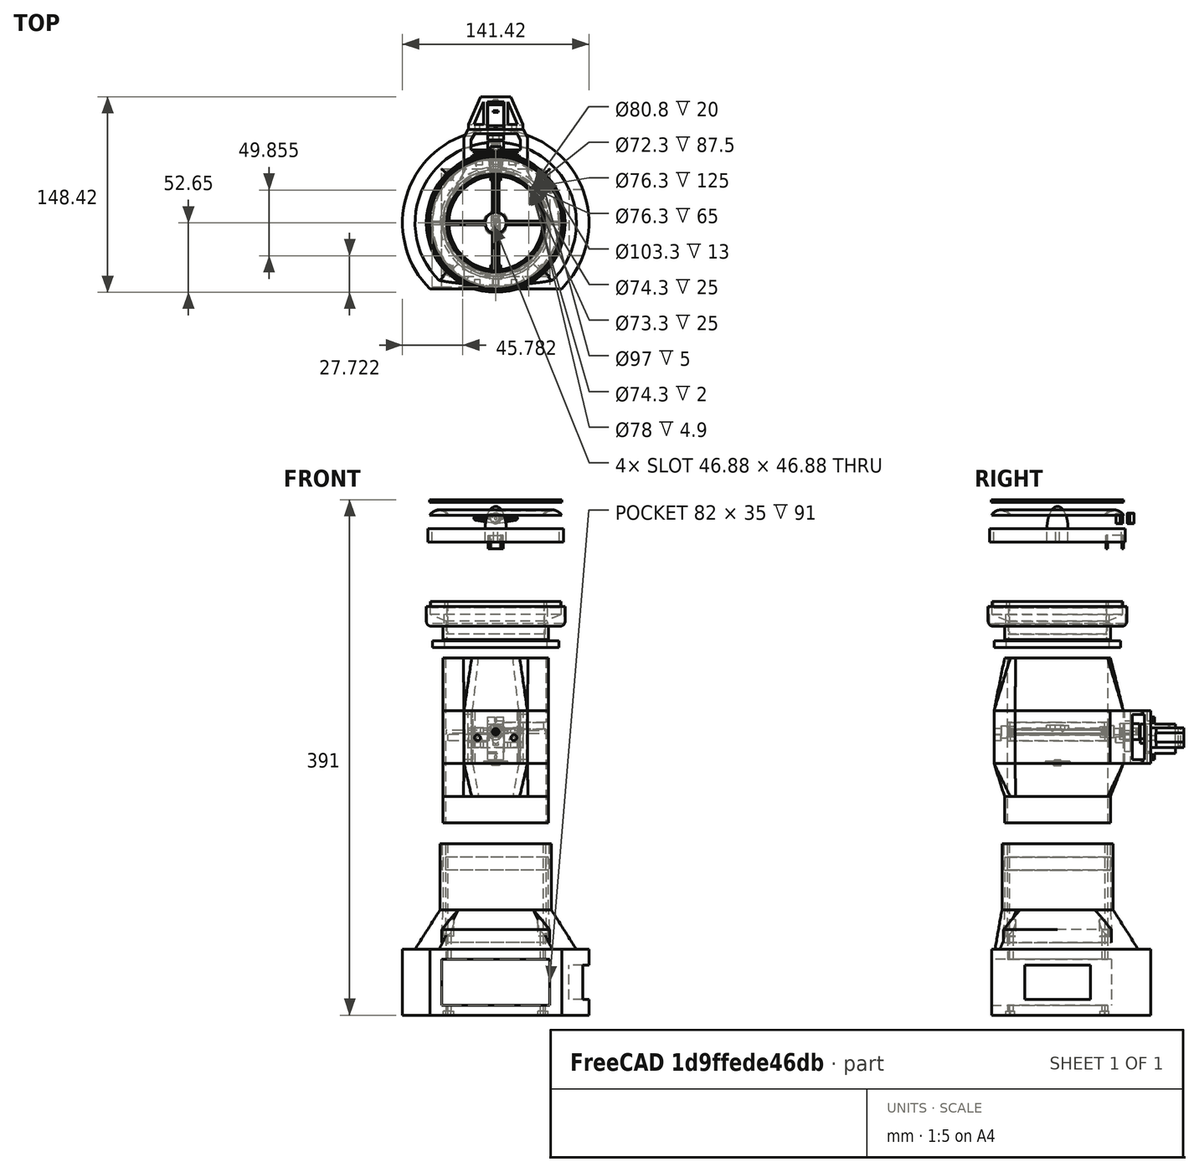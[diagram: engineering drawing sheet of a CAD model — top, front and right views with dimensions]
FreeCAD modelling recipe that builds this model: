
FCSTD DOCUMENT  (FreeCAD 0.20R29177 (Git))
Label: WindSim (1) (2) (1) (1)
License: All rights reserved
LicenseURL: http://en.wikipedia.org/wiki/All_rights_reserved
objects: Sketcher::SketchObject×66, PartDesign::Pocket×28, PartDesign::Pad×23, PartDesign::Body×14, PartDesign::AdditiveLoft×5, PartDesign::Mirrored×4, Part::Feature×4, App::DocumentObjectGroup×3, PartDesign::Revolution×2, Part::Part2DObjectPython×1, PartDesign::PolarPattern×1, PartDesign::Fillet×1, Spreadsheet::Sheet×1, Mesh::Feature×1
note: 208 computed .brp shape members not serialized (recipe doc carries the construction recipe); baked Part::Feature solids carry a one-line shape summary decoded from their .brp

FEATURE [Sketcher::SketchObject] Sketch004  label="sk_flap_base"
  FullyConstrained = true
  MapMode = 5
  Support = -> [XY_Plane001]
  expr: .Constraints.flap_diameter = <<Spreadsheet>>.flap_diameter
  sketch-geometry (1):
    g0: Circle CenterX=0 CenterY=0 CenterZ=0 NormalX=0 NormalY=0 NormalZ=1 AngleXU=0 Radius=37.65
  constraints (2):
    c: Coincident(g0,g-1)
    c: Diameter(g0) = 75.3  'flap_diameter'
FEATURE [PartDesign::Pad] Pad002  label="pad_flap_base"
  Direction = (0,0,1)
  Length = 2
  Length2 = 10
  Profile = -> Sketch004
  Type = 0
  expr: Length = <<Spreadsheet>>.flap_width
FEATURE [Sketcher::SketchObject] Sketch005  label="sk_flap_rod"
  AttachmentOffset = pos=(0,1,0) rot=(0,0,1;0rad)
  FullyConstrained = true
  MapMode = 5
  Placement = pos=(-2e-16,2e-16,1) rot=(0.57735,0.57735,0.57735;2.0944rad)
  Support = -> [YZ_Plane001]
  expr: .AttachmentOffset.Base.y = <<pad_flap_base>>.Length / 2
  expr: .Constraints.flap_rod_hole_diameter = <<Spreadsheet>>.flap_rod_hole_diameter
  expr: .Constraints.flap_rod_outer_diameter = <<Spreadsheet>>.flap_rod_hole_diameter + <<Spreadsheet>>.flap_rod_width
  sketch-geometry (2):
    g0: Circle CenterX=0 CenterY=0 CenterZ=0 NormalX=0 NormalY=0 NormalZ=1 AngleXU=0 Radius=1.75
    g1: Circle CenterX=0 CenterY=0 CenterZ=0 NormalX=0 NormalY=0 NormalZ=1 AngleXU=0 Radius=2.75
  constraints (4):
    c: Coincident(g0,g-1)
    c: Coincident(g1,g0)
    c: Diameter(g0) = 3.5  'flap_rod_hole_diameter'
    c: Diameter(g1) = 5.5  'flap_rod_outer_diameter'
FEATURE [PartDesign::Pad] Pad003  label="pad_flap_rod"
  BaseFeature = -> Pad002
  Direction = (1,-2e-16,3e-16)
  Length = 65.3
  Length2 = 10
  Midplane = true
  Profile = -> Sketch005
  Type = 0
  expr: Length = <<Spreadsheet>>.flap_diameter - 10mm
FEATURE [Sketcher::SketchObject] Sketch006  label="sk_flap_rod_hole_through"
  AttachmentOffset = pos=(0,1,37.65) rot=(0,0,1;0rad)
  FullyConstrained = true
  MapMode = 5
  Placement = pos=(37.65,-8.1e-15,1) rot=(0.57735,0.57735,0.57735;2.0944rad)
  Support = -> [YZ_Plane001]
  expr: .AttachmentOffset.Base.y = <<pad_flap_base>>.Length / 2
  expr: .AttachmentOffset.Base.z = <<sk_flap_base>>.Constraints.flap_diameter / 2
  expr: .Constraints.flap_rod_hole_diameter = <<sk_flap_rod>>.Constraints.flap_rod_hole_diameter
  sketch-geometry (1):
    g0: Circle CenterX=0 CenterY=0 CenterZ=0 NormalX=0 NormalY=0 NormalZ=1 AngleXU=0 Radius=1.75
  constraints (2):
    c: Coincident(g0,g-1)
    c: Diameter(g0) = 3.5  'flap_rod_hole_diameter'
FEATURE [Sketcher::SketchObject] Sketch007  label="sk_flap_rod_hold"
  AttachmentOffset = pos=(0,1,37.15) rot=(0,0,1;0rad)
  FullyConstrained = true
  MapMode = 5
  Placement = pos=(37.15,-8e-15,1) rot=(0.57735,0.57735,0.57735;2.0944rad)
  Support = -> [YZ_Plane001]
  expr: .AttachmentOffset.Base.y = <<pad_flap_base>>.Length / 2
  expr: .AttachmentOffset.Base.z = <<sk_flap_base>>.Constraints.flap_diameter / 2 - 0.5mm
  expr: Constraints[1] = <<Spreadsheet>>.flap_rod_nut_width + 2mm
  sketch-geometry (1):
    g0: Circle CenterX=0 CenterY=0 CenterZ=0 NormalX=0 NormalY=0 NormalZ=1 AngleXU=0 Radius=4.05
  constraints (2):
    c: Coincident(g0,g-1)
    c: Diameter(g0) = 8.1
FEATURE [PartDesign::Pad] Pad004  label="pad_flap_hold"
  BaseFeature = -> Pad003
  Direction = (1,-2e-16,3e-16)
  Length = 5
  Length2 = 10
  Profile = -> Sketch007
  Reversed = true
  Type = 0
FEATURE [Sketcher::SketchObject] Sketch008  label="sk_flap_nut_hold"
  AttachmentOffset = pos=(0,1,37.65) rot=(0,0,1;0rad)
  FullyConstrained = true
  MapMode = 5
  Placement = pos=(37.65,-8.1e-15,1) rot=(0.57735,0.57735,0.57735;2.0944rad)
  Support = -> [YZ_Plane001]
  expr: .AttachmentOffset.Base.y = <<pad_flap_base>>.Length / 2
  expr: .AttachmentOffset.Base.z = <<sk_flap_base>>.Constraints.flap_diameter / 2
  expr: Constraints[19] = <<Spreadsheet>>.flap_rod_nut_width
  sketch-geometry (7):
    g0: LineSegment StartX=1.525 StartY=-2.64138 StartZ=0 EndX=3.05 EndY=4e-16 EndZ=0
    g1: LineSegment StartX=3.05 StartY=4e-16 StartZ=0 EndX=1.525 EndY=2.64138 EndZ=0
    g2: LineSegment StartX=1.525 StartY=2.64138 StartZ=0 EndX=-1.525 EndY=2.64138 EndZ=0
    g3: LineSegment StartX=-1.525 StartY=2.64138 StartZ=0 EndX=-3.05 EndY=4e-16 EndZ=0
    g4: LineSegment StartX=-3.05 StartY=4e-16 StartZ=0 EndX=-1.525 EndY=-2.64138 EndZ=0
    g5: LineSegment StartX=-1.525 StartY=-2.64138 StartZ=0 EndX=1.525 EndY=-2.64138 EndZ=0
    g6: Circle CenterX=0 CenterY=0 CenterZ=0 NormalX=0 NormalY=0 NormalZ=1 AngleXU=0 Radius=3.05
  constraints (16):
    c: Coincident(g0,g1)
    c: Coincident(g1,g2)
    c: Coincident(g2,g3)
    c: Coincident(g3,g4)
    c: Coincident(g4,g5)
    c: Coincident(g5,g0)
    c: Equal(g0, g1-g5) x5
    c: PointOnObject(g0,g6)
    c: PointOnObject(g1,g6)
    c: PointOnObject(g2,g6)
    c: PointOnObject(g3,g6)
    c: PointOnObject(g4,g6)
    c: PointOnObject(g5,g6)
    c: Coincident(g6,g-1)
    c: Horizontal(g5)
    c: DistanceX(g3,g0) = 6.1
FEATURE [PartDesign::Mirrored] Mirrored  label="mirror_flap_hold"
  BaseFeature = -> Pad004
  MirrorPlane = -> YZ_Plane001
  Originals = -> [Pad004]
FEATURE [PartDesign::Pocket] Pocket  label="pocket_nut_hold"
  BaseFeature = -> Mirrored
  Direction = (-1,2e-16,-3e-16)
  Length = 4
  Length2 = 5
  Profile = -> Sketch008
  Type = 0
FEATURE [PartDesign::Mirrored] Mirrored001  label="mirror_pocket_nut_hold"
  BaseFeature = -> Pocket
  MirrorPlane = -> YZ_Plane001
  Originals = -> [Pocket]
FEATURE [Sketcher::SketchObject] Sketch009  label="sk_valve_base"
  FullyConstrained = true
  MapMode = 5
  Support = -> [XY_Plane002]
  expr: Constraints[1] = <<sk_fanduct_base>>.Constraints.duct_hole_diameter
  expr: Constraints[3] = <<sk_pipe>>.Constraints.pipe_outer_diameter
  sketch-geometry (11):
    g0: Circle CenterX=0 CenterY=0 CenterZ=0 NormalX=0 NormalY=0 NormalZ=1 AngleXU=0 Radius=38.15
    g1: ArcOfCircle CenterX=0 CenterY=0 CenterZ=0 NormalX=0 NormalY=0 NormalZ=1 AngleXU=0 Radius=40.15 StartAngle=2.61815 EndAngle=4.07013
    g2: LineSegment StartX=17.5 StartY=50 StartZ=0 EndX=-17.5 EndY=50 EndZ=0
    g3: LineSegment StartX=-24.0499 StartY=-32.15 StartZ=0 EndX=-24.0499 EndY=-48.15 EndZ=0
    g4: LineSegment StartX=24.0499 StartY=-32.15 StartZ=0 EndX=24.0499 EndY=-48.15 EndZ=0
    g5: LineSegment StartX=24.0499 StartY=-48.15 StartZ=0 EndX=-24.0499 EndY=-48.15 EndZ=0
    g6: ArcOfCircle CenterX=0 CenterY=0 CenterZ=0 NormalX=0 NormalY=0 NormalZ=1 AngleXU=0 Radius=40.15 StartAngle=5.35464 EndAngle=6.80663
    g7: GeomPoint X=0 Y=38.15 Z=0
    g8: GeomPoint X=0 Y=-38.15 Z=0
    g9: LineSegment StartX=-17.5 StartY=50 StartZ=0 EndX=-34.7741 EndY=20.0695 EndZ=0
    g10: LineSegment StartX=17.5 StartY=50 StartZ=0 EndX=34.7741 EndY=20.0695 EndZ=0
  constraints (29):
    c: Coincident(g0,g-1)
    c: Diameter(g0) = 76.3
    c: Coincident(g1,g0)
    c: Diameter(g1) = 80.3
    c: Vertical(g3)
    c: Vertical(g4)
    c: Coincident(g5,g4)
    c: Coincident(g5,g3)
    c: Horizontal(g5)
    c: Symmetric(g4,g3,g-2)
    c: PointOnObject(g6,g4)
    c: Coincident(g1,g6)
    c: DistanceY(g4,g4) = 16  'bottom_hold_height'
    c: PointOnObject(g7,g0)
    c: PointOnObject(g7,g-2)
    c: PointOnObject(g8,g0)
    c: PointOnObject(g8,g-2)
    c: DistanceY(g3,g8) = 10
    c: DistanceY(g0,g2) = 50  'top_border'
    c: DistanceY(g4,g0) = 48.15  'bottom_border'
    c: Tangent(g1,g9) = -1.5708
    c: Tangent(g6,g10) = 1.5708
    c: Coincident(g9,g2)
    c: Coincident(g10,g2)
    c: Coincident(g3,g1)
    c: Horizontal(g2)
    c: Symmetric(g1,g6,g-2)
    c: DistanceX(g2,g2) = 35  'top_width'
    c: Angle(g9,g2) = 2.09424  'top_angle'
FEATURE [PartDesign::Pad] Pad005  label="pad_valve_base"
  Direction = (0,0,1)
  Length = 40
  Length2 = 10
  Profile = -> Sketch009
  Type = 0
FEATURE [Sketcher::SketchObject] Sketch011  label="sk_valve_front_taper"
  AttachmentOffset = pos=(0,0,80) rot=(0,0,1;0rad)
  FullyConstrained = true
  MapMode = 5
  Placement = pos=(0,0,80) rot=(0,0,1;0rad)
  Support = -> [XY_Plane002]
  expr: .AttachmentOffset.Base.z = <<pad_valve_base>>.Length + 40mm
  expr: Constraints[2] = <<sk_fanduct_base>>.Constraints.duct_hole_diameter
  expr: Constraints[3] = <<sk_pipe>>.Constraints.pipe_outer_diameter
  sketch-geometry (2):
    g0: Circle CenterX=0 CenterY=0 CenterZ=0 NormalX=0 NormalY=0 NormalZ=1 AngleXU=0 Radius=38.15
    g1: Circle CenterX=0 CenterY=0 CenterZ=0 NormalX=0 NormalY=0 NormalZ=1 AngleXU=0 Radius=40.15
  constraints (4):
    c: Coincident(g0,g-1)
    c: Coincident(g1,g0)
    c: Diameter(g0) = 76.3
    c: Diameter(g1) = 80.3
FEATURE [Part::Feature] Fusion007001  label="Servo-sg90-final"
  Placement = pos=(0,89.6,7.5) rot=(1,0,0;1.5708rad)
  shape: bbox 11.8 x 29.9 x 32.4 mm, 77 faces (baked)
FEATURE [Part::Feature] Pocket003001  label="Final-2-arms-horn"
  Placement = pos=(0,53,186) rot=(-1,0,0;1.5708rad)
  shape: bbox 33 x 5 x 8 mm, 28 faces (baked)
FEATURE [Part::Feature] Pocket003002  label="Final-2-arms-horn001"
  Placement = pos=(0,49.5,186) rot=(0,0.707107,-0.707107;3.14159rad)
  shape: bbox 33 x 5 x 8 mm, 28 faces (baked)
FEATURE [Sketcher::SketchObject] Sketch012  label="sk_valve_main_axis"
  AttachmentOffset = pos=(0,24,-50) rot=(0,0,1;0rad)
  FullyConstrained = true
  MapMode = 5
  Placement = pos=(0,50,24) rot=(1,0,0;1.5708rad)
  Support = -> [XZ_Plane002]
  expr: .AttachmentOffset.Base.z = Sketch009.Constraints.top_border * -1
  sketch-geometry (1):
    g0: Circle CenterX=0 CenterY=0 CenterZ=0 NormalX=0 NormalY=0 NormalZ=1 AngleXU=0 Radius=2.45
  constraints (2):
    c: Coincident(g0,g-1)
    c: Diameter(g0) = 4.9  'main_axis_diameter'
FEATURE [Sketcher::SketchObject] Sketch014  label="sk_bearing_top"
  AttachmentOffset = pos=(0,24,-37.65) rot=(0,0,1;0rad)
  FullyConstrained = true
  MapMode = 5
  Placement = pos=(0,37.65,24) rot=(1,0,0;1.5708rad)
  Support = -> [XZ_Plane002]
  expr: .AttachmentOffset.Base.z = <<sk_fanduct_base>>.Constraints.duct_hole_diameter / 2 * -1 + 0.5mm
  sketch-geometry (1):
    g0: Circle CenterX=0 CenterY=0 CenterZ=0 NormalX=0 NormalY=0 NormalZ=1 AngleXU=0 Radius=4.5
  constraints (2):
    c: Coincident(g0,g-1)
    c: Diameter(g0) = 9  'bearing_diameter'
FEATURE [PartDesign::Pocket] Pocket003003  label="pocket_valve_main_axis"
  BaseFeature = -> Pad005
  Direction = (0,1,2e-16)
  Length = 2
  Length2 = 5
  Midplane = true
  Profile = -> Sketch012
  Type = 1
FEATURE [PartDesign::Pocket] Pocket003004  label="pocket_bearing_top"
  BaseFeature = -> Pocket003003
  Direction = (0,1,2e-16)
  Length = 5
  Length2 = 5
  Profile = -> Sketch014
  Type = 0
FEATURE [Sketcher::SketchObject] Sketch015  label="sk_bearing_bottom"
  AttachmentOffset = pos=(0,24,37.65) rot=(0,0,1;0rad)
  FullyConstrained = true
  MapMode = 5
  Placement = pos=(0,-37.65,24) rot=(1,0,0;1.5708rad)
  Support = -> [XZ_Plane002]
  expr: .AttachmentOffset.Base.z = <<sk_fanduct_base>>.Constraints.duct_hole_diameter / 2 - 0.5mm
  expr: Constraints[1] = <<sk_bearing_top>>.Constraints.bearing_diameter
  sketch-geometry (1):
    g0: Circle CenterX=0 CenterY=0 CenterZ=0 NormalX=0 NormalY=0 NormalZ=1 AngleXU=0 Radius=4.5
  constraints (2):
    c: Coincident(g0,g-1)
    c: Diameter(g0) = 9
FEATURE [PartDesign::Pocket] Pocket003005  label="pocket_bearing_bottom"
  BaseFeature = -> Pocket003004
  Direction = (0,1,2e-16)
  Length = 5
  Length2 = 5
  Profile = -> Sketch015
  Reversed = true
  Type = 0
FEATURE [Sketcher::SketchObject] Sketch016  label="sk_valve_back_taper"
  AttachmentOffset = pos=(0,0,-25) rot=(0,0,1;0rad)
  FullyConstrained = true
  MapMode = 5
  Placement = pos=(0,0,-25) rot=(0,0,1;0rad)
  Support = -> [XY_Plane002]
  expr: Constraints[2] = <<sk_fanduct_base>>.Constraints.duct_hole_diameter
  expr: Constraints[3] = <<sk_pipe>>.Constraints.pipe_outer_diameter
  sketch-geometry (2):
    g0: Circle CenterX=0 CenterY=0 CenterZ=0 NormalX=0 NormalY=0 NormalZ=1 AngleXU=0 Radius=38.15
    g1: Circle CenterX=0 CenterY=0 CenterZ=0 NormalX=0 NormalY=0 NormalZ=1 AngleXU=0 Radius=40.15
  constraints (4):
    c: Coincident(g0,g-1)
    c: Coincident(g1,g0)
    c: Diameter(g0) = 76.3
    c: Diameter(g1) = 80.3
FEATURE [Part::Feature] Part__Feature  label="shaft-drill"
  shape: bbox 18.7 x 18.7 x 4.1 mm, 22 faces (baked)
FEATURE [Sketcher::SketchObject] Sketch020
  FullyConstrained = true
  MapMode = 5
  Support = -> [XY_Plane003]
  sketch-geometry (1):
    g0: Circle CenterX=0 CenterY=0 CenterZ=0 NormalX=0 NormalY=0 NormalZ=1 AngleXU=0 Radius=6
  constraints (2):
    c: Coincident(g0,g-1)
    c: Diameter(g0) = 12  'aussendurchmesser'
FEATURE [PartDesign::Pad] Pad008
  Direction = (1,1,1)
  Length = 3
  Length2 = 100
  Profile = -> Sketch020
  Type = 0
FEATURE [Part::Part2DObjectPython] InvoluteGear  # Draft 2D object (typed FeaturePython)
  ExternalGear = true
  HighPrecision = true
  Modules = 0.19
  NumberOfTeeth = 24
  PressureAngle = 28
FEATURE [PartDesign::Pocket] Pocket003007
  BaseFeature = -> Pad008
  Direction = (1,1,1)
  Length = 5
  Length2 = 100
  Profile = -> InvoluteGear
  Reversed = true
  Type = 1
FEATURE [Sketcher::SketchObject] Sketch021
  AttachmentOffset = pos=(0,0,3) rot=(0,0,1;0rad)
  FullyConstrained = true
  MapMode = 5
  Placement = pos=(0,0,3) rot=(0,0,1;0rad)
  Support = -> [XY_Plane003]
  expr: .AttachmentOffset.Base.z = <<Pad008>>.Length
  expr: Constraints[1] = <<Sketch020>>.Constraints.aussendurchmesser
  sketch-geometry (1):
    g0: Circle CenterX=0 CenterY=0 CenterZ=0 NormalX=0 NormalY=0 NormalZ=1 AngleXU=0 Radius=6
  constraints (2):
    c: Coincident(g0,g-1)
    c: Diameter(g0) = 12
FEATURE [PartDesign::Pad] Pad009
  BaseFeature = -> Pocket003007
  Direction = (1,1,1)
  Length = 12
  Length2 = 100
  Profile = -> Sketch021
  Type = 0
FEATURE [Sketcher::SketchObject] Sketch022
  AttachmentOffset = pos=(0,0,15) rot=(0,0,1;0rad)
  FullyConstrained = true
  MapMode = 5
  Placement = pos=(0,0,15) rot=(0,0,1;0rad)
  Support = -> [XY_Plane003]
  expr: .AttachmentOffset.Base.z = <<Pad008>>.Length + <<Pad009>>.Length
  sketch-geometry (7):
    g0: LineSegment StartX=1.525 StartY=-2.64138 StartZ=0 EndX=3.05 EndY=-1.332e-13 EndZ=0
    g1: LineSegment StartX=3.05 StartY=-1.332e-13 StartZ=0 EndX=1.525 EndY=2.64138 EndZ=0
    g2: LineSegment StartX=1.525 StartY=2.64138 StartZ=0 EndX=-1.525 EndY=2.64138 EndZ=0
    g3: LineSegment StartX=-1.525 StartY=2.64138 StartZ=0 EndX=-3.05 EndY=-1.248e-13 EndZ=0
    g4: LineSegment StartX=-3.05 StartY=-1.248e-13 StartZ=0 EndX=-1.525 EndY=-2.64138 EndZ=0
    g5: LineSegment StartX=-1.525 StartY=-2.64138 StartZ=0 EndX=1.525 EndY=-2.64138 EndZ=0
    g6: Circle CenterX=0 CenterY=0 CenterZ=0 NormalX=0 NormalY=0 NormalZ=1 AngleXU=0 Radius=3.05
  constraints (16):
    c: Coincident(g0,g1)
    c: Coincident(g1,g2)
    c: Coincident(g2,g3)
    c: Coincident(g3,g4)
    c: Coincident(g4,g5)
    c: Coincident(g5,g0)
    c: Equal(g0, g1-g5) x5
    c: PointOnObject(g0,g6)
    c: PointOnObject(g1,g6)
    c: PointOnObject(g2,g6)
    c: PointOnObject(g3,g6)
    c: PointOnObject(g4,g6)
    c: PointOnObject(g5,g6)
    c: Coincident(g6,g-1)
    c: Horizontal(g5)
    c: DistanceX(g3,g0) = 6.1
FEATURE [PartDesign::Pocket] Pocket003008
  BaseFeature = -> Pad009
  Direction = (1,1,1)
  Length = 7
  Length2 = 100
  Profile = -> Sketch022
  Type = 0
FEATURE [Sketcher::SketchObject] Sketch023
  AttachmentOffset = pos=(0,0,8) rot=(0,0,1;0rad)
  FullyConstrained = true
  MapMode = 5
  Placement = pos=(0,0,8) rot=(0,0,1;0rad)
  Support = -> [XY_Plane003]
  expr: .AttachmentOffset.Base.z = <<Pad008>>.Length + <<Pad009>>.Length - <<Pocket003008>>.Length
  sketch-geometry (1):
    g0: Circle CenterX=0 CenterY=0 CenterZ=0 NormalX=0 NormalY=0 NormalZ=1 AngleXU=0 Radius=1
  constraints (2):
    c: Coincident(g0,g-1)
    c: Diameter(g0) = 2
FEATURE [PartDesign::Pocket] Pocket003009
  BaseFeature = -> Pocket003008
  Direction = (1,1,1)
  Length = 4.8
  Length2 = 100
  Profile = -> Sketch023
  Type = 1
  expr: Length = 2.4 * 2
FEATURE [Sketcher::SketchObject] Sketch024
  ExternalGeometry = -> [Pocket003009]
  FullyConstrained = true
  MapMode = 5
  Support = -> [XY_Plane003]
  constraints (1):
    c: Distance(g-3,g-4) = 4.93975
FEATURE [PartDesign::Body] Body003  label="Servo_shaft_adapter"
  Group = -> [Sketch020,Pad008,InvoluteGear,Pocket003007,Sketch021,Pad009,Sketch022,Pocket003008,Sketch023,Pocket003009,Sketch024]
  Origin = -> Origin003
  Placement = pos=(0,47.3,24.1) rot=(-1,0,0;1.5708rad)
  Tip = -> Pocket003009
FEATURE [Sketcher::SketchObject] Sketch029  label="sk_valve_front"
  AttachmentOffset = pos=(0,0,40) rot=(0,0,1;0rad)
  FullyConstrained = true
  MapMode = 5
  Placement = pos=(0,0,40) rot=(0,0,1;0rad)
  Support = -> [XY_Plane002]
  expr: .AttachmentOffset.Base.z = <<pad_valve_base>>.Length
  expr: Constraints[1] = <<sk_fanduct_base>>.Constraints.duct_hole_diameter
  expr: Constraints[3] = <<sk_pipe>>.Constraints.pipe_outer_diameter
  sketch-geometry (11):
    g0: Circle CenterX=0 CenterY=0 CenterZ=0 NormalX=0 NormalY=0 NormalZ=1 AngleXU=0 Radius=38.15
    g1: ArcOfCircle CenterX=0 CenterY=0 CenterZ=0 NormalX=0 NormalY=0 NormalZ=1 AngleXU=0 Radius=40.15 StartAngle=2.61815 EndAngle=4.07013
    g2: LineSegment StartX=17.5 StartY=50 StartZ=0 EndX=-17.5 EndY=50 EndZ=0
    g3: LineSegment StartX=-24.0499 StartY=-32.15 StartZ=0 EndX=-24.0499 EndY=-48.15 EndZ=0
    g4: LineSegment StartX=24.0499 StartY=-32.15 StartZ=0 EndX=24.0499 EndY=-48.15 EndZ=0
    g5: LineSegment StartX=24.0499 StartY=-48.15 StartZ=0 EndX=-24.0499 EndY=-48.15 EndZ=0
    g6: ArcOfCircle CenterX=0 CenterY=0 CenterZ=0 NormalX=0 NormalY=0 NormalZ=1 AngleXU=0 Radius=40.15 StartAngle=5.35464 EndAngle=6.80663
    g7: GeomPoint X=0 Y=38.15 Z=0
    g8: GeomPoint X=0 Y=-38.15 Z=0
    g9: LineSegment StartX=-17.5 StartY=50 StartZ=0 EndX=-34.7741 EndY=20.0695 EndZ=0
    g10: LineSegment StartX=17.5 StartY=50 StartZ=0 EndX=34.7741 EndY=20.0695 EndZ=0
  constraints (28):
    c: Coincident(g0,g-1)
    c: Diameter(g0) = 76.3
    c: Coincident(g1,g0)
    c: Diameter(g1) = 80.3
    c: Vertical(g3)
    c: Vertical(g4)
    c: Coincident(g5,g4)
    c: Coincident(g5,g3)
    c: Horizontal(g5)
    c: Symmetric(g4,g3,g-2)
    c: PointOnObject(g6,g4)
    c: Coincident(g1,g6)
    c: DistanceY(g4,g4) = 16  'bottom_hold_height'
    c: PointOnObject(g7,g0)
    c: PointOnObject(g7,g-2)
    c: PointOnObject(g8,g0)
    c: PointOnObject(g8,g-2)
    c: DistanceY(g3,g8) = 10
    c: DistanceY(g0,g2) = 50  'top_border'
    c: DistanceY(g4,g0) = 48.15  'bottom_border'
    c: Tangent(g1,g9) = -1.5708
    c: Tangent(g6,g10) = 1.5708
    c: Coincident(g9,g2)
    c: Coincident(g10,g2)
    c: Coincident(g3,g1)
    c: Horizontal(g2)
    c: Symmetric(g1,g6,g-2)
    c: DistanceX(g2,g2) = 35  'top_width'
FEATURE [Sketcher::SketchObject] Sketch030  label="sk_flap_counter_right"
  AttachmentOffset = pos=(0,0,26) rot=(0,0,1;0rad)
  FullyConstrained = true
  MapMode = 5
  Placement = pos=(0,0,26) rot=(0,0,1;0rad)
  Support = -> [XY_Plane002]
  expr: Constraints[5] = <<sk_pipe>>.Constraints.pipe_outer_diameter
  sketch-geometry (4):
    g0: ArcOfCircle CenterX=0 CenterY=1.3e-15 CenterZ=0 NormalX=0 NormalY=0 NormalZ=1 AngleXU=0 Radius=40.15 StartAngle=4.83725 EndAngle=7.72912
    g1: ArcOfCircle CenterX=0 CenterY=1.3e-15 CenterZ=0 NormalX=0 NormalY=0 NormalZ=1 AngleXU=0 Radius=36.1846 StartAngle=4.85101 EndAngle=7.71536
    g2: LineSegment StartX=5 StartY=39.8375 StartZ=0 EndX=5 EndY=35.8375 EndZ=0
    g3: LineSegment StartX=5 StartY=-39.8375 StartZ=0 EndX=5 EndY=-35.8375 EndZ=0
  constraints (12):
    c: Coincident(g1,g0)
    c: Coincident(g2,g0)
    c: Coincident(g2,g1)
    c: Coincident(g3,g0)
    c: Coincident(g3,g1)
    c: Diameter(g0) = 80.3
    c: Symmetric(g1,g1,g-1)
    c: Vertical(g2)
    c: Vertical(g3)
    c: DistanceY(g2,g2) = 4  'inner_pad_height'
    c: DistanceX(g0,g0) = 5  'inner_pad_distance'
    c: Coincident(g0,g-1)
FEATURE [Sketcher::SketchObject] Sketch031  label="sk_flap_counter_left"
  AttachmentOffset = pos=(0,0,22) rot=(0,0,1;0rad)
  FullyConstrained = true
  MapMode = 5
  Placement = pos=(0,0,22) rot=(0,0,1;0rad)
  Support = -> [XY_Plane002]
  expr: Constraints[7] = <<sk_flap_counter_right>>.Constraints.inner_pad_height
  expr: Constraints[8] = <<sk_flap_counter_right>>.Constraints.inner_pad_distance
  expr: Constraints[9] = <<sk_pipe>>.Constraints.pipe_outer_diameter
  sketch-geometry (4):
    g0: ArcOfCircle CenterX=0 CenterY=-2.5e-15 CenterZ=0 NormalX=0 NormalY=0 NormalZ=1 AngleXU=0 Radius=36.1846 StartAngle=1.70942 EndAngle=4.57376
    g1: ArcOfCircle CenterX=0 CenterY=-2.5e-15 CenterZ=0 NormalX=0 NormalY=0 NormalZ=1 AngleXU=0 Radius=40.15 StartAngle=1.69565 EndAngle=4.58753
    g2: LineSegment StartX=-5 StartY=39.8375 StartZ=0 EndX=-5 EndY=35.8375 EndZ=0
    g3: LineSegment StartX=-5 StartY=-39.8375 StartZ=0 EndX=-5 EndY=-35.8375 EndZ=0
  constraints (12):
    c: Coincident(g1,g0)
    c: Coincident(g2,g1)
    c: Coincident(g2,g0)
    c: Coincident(g3,g1)
    c: Coincident(g3,g0)
    c: Vertical(g3)
    c: Vertical(g2)
    c: DistanceY(g2,g2) = 4
    c: DistanceX(g0,g0) = 5
    c: Diameter(g1) = 80.3
    c: Symmetric(g0,g0,g-1)
    c: Coincident(g0,g-1)
FEATURE [Sketcher::SketchObject] Sketch033  label="sk_valve_top_connect_holes"
  AttachmentOffset = pos=(0,0,49) rot=(0,0,1;0rad)
  FullyConstrained = true
  MapMode = 5
  Placement = pos=(0,-49,-1.09e-14) rot=(1,0,0;1.5708rad)
  Support = -> [XZ_Plane002]
  expr: Constraints[2] = <<Spreadsheet>>.m3_inlay_width
  sketch-geometry (2):
    g0: Circle CenterX=-13.83 CenterY=19.55 CenterZ=0 NormalX=0 NormalY=0 NormalZ=1 AngleXU=0 Radius=2.24
    g1: Circle CenterX=13.83 CenterY=19.55 CenterZ=0 NormalX=0 NormalY=0 NormalZ=1 AngleXU=0 Radius=2.24
  constraints (5):
    c: Symmetric(g0,g1,g-2)
    c: Equal(g0,g1)
    c: Diameter(g0) = 4.48
    c: DistanceX(g0,g-1) = 13.83  'center_distance'
    c: DistanceY(g-1,g0) = 19.55  'rear_distance'
FEATURE [Sketcher::SketchObject] Sketch034  label="sk_valve_bottom_connect_holes"
  AttachmentOffset = pos=(0,0,-50) rot=(0,0,1;0rad)
  FullyConstrained = true
  MapMode = 5
  Placement = pos=(0,50,1.11e-14) rot=(1,0,0;1.5708rad)
  Support = -> [XZ_Plane002]
  expr: Constraints[0] = <<Spreadsheet>>.m3_inlay_width
  sketch-geometry (2):
    g0: Circle CenterX=-12.49 CenterY=18.07 CenterZ=0 NormalX=0 NormalY=0 NormalZ=1 AngleXU=0 Radius=2.24
    g1: Circle CenterX=12.49 CenterY=18.07 CenterZ=0 NormalX=0 NormalY=0 NormalZ=1 AngleXU=0 Radius=2.24
  constraints (5):
    c: Diameter(g0) = 4.48
    c: Equal(g1,g0)
    c: Symmetric(g1,g0,g-2)
    c: DistanceX(g0,g-1) = 12.49  'center_distance'
    c: DistanceY(g-1,g0) = 18.07  'rear_distance'
FEATURE [Sketcher::SketchObject] Sketch028  label="sk_valve_back"
  FullyConstrained = true
  MapMode = 5
  Support = -> [XY_Plane002]
  expr: Constraints[1] = <<sk_fanduct_base>>.Constraints.duct_hole_diameter
  expr: Constraints[3] = <<sk_pipe>>.Constraints.pipe_outer_diameter
  sketch-geometry (11):
    g0: Circle CenterX=0 CenterY=0 CenterZ=0 NormalX=0 NormalY=0 NormalZ=1 AngleXU=0 Radius=38.15
    g1: ArcOfCircle CenterX=0 CenterY=0 CenterZ=0 NormalX=0 NormalY=0 NormalZ=1 AngleXU=0 Radius=40.15 StartAngle=2.61815 EndAngle=4.07013
    g2: LineSegment StartX=17.5 StartY=50 StartZ=0 EndX=-17.5 EndY=50 EndZ=0
    g3: LineSegment StartX=-24.0499 StartY=-32.15 StartZ=0 EndX=-24.0499 EndY=-48.15 EndZ=0
    g4: LineSegment StartX=24.0499 StartY=-32.15 StartZ=0 EndX=24.0499 EndY=-48.15 EndZ=0
    g5: LineSegment StartX=24.0499 StartY=-48.15 StartZ=0 EndX=-24.0499 EndY=-48.15 EndZ=0
    g6: ArcOfCircle CenterX=0 CenterY=0 CenterZ=0 NormalX=0 NormalY=0 NormalZ=1 AngleXU=0 Radius=40.15 StartAngle=5.35464 EndAngle=6.80663
    g7: GeomPoint X=0 Y=38.15 Z=0
    g8: GeomPoint X=0 Y=-38.15 Z=0
    g9: LineSegment StartX=-17.5 StartY=50 StartZ=0 EndX=-34.7741 EndY=20.0695 EndZ=0
    g10: LineSegment StartX=17.5 StartY=50 StartZ=0 EndX=34.7741 EndY=20.0695 EndZ=0
  constraints (28):
    c: Coincident(g0,g-1)
    c: Diameter(g0) = 76.3
    c: Coincident(g1,g0)
    c: Diameter(g1) = 80.3
    c: Vertical(g3)
    c: Vertical(g4)
    c: Coincident(g5,g4)
    c: Coincident(g5,g3)
    c: Horizontal(g5)
    c: Symmetric(g4,g3,g-2)
    c: PointOnObject(g6,g4)
    c: Coincident(g1,g6)
    c: DistanceY(g4,g4) = 16  'bottom_hold_height'
    c: PointOnObject(g7,g0)
    c: PointOnObject(g7,g-2)
    c: PointOnObject(g8,g0)
    c: PointOnObject(g8,g-2)
    c: DistanceY(g3,g8) = 10
    c: DistanceY(g0,g2) = 50  'top_border'
    c: DistanceY(g4,g0) = 48.15  'bottom_border'
    c: Tangent(g1,g9) = -1.5708
    c: Tangent(g6,g10) = 1.5708
    c: Coincident(g9,g2)
    c: Coincident(g10,g2)
    c: Coincident(g3,g1)
    c: Horizontal(g2)
    c: Symmetric(g1,g6,g-2)
    c: DistanceX(g2,g2) = 35  'top_width'
FEATURE [PartDesign::AdditiveLoft] AdditiveLoft001  label="loft_back"
  BaseFeature = -> Pocket003005
  Closed = true
  Profile = -> Sketch028
  Refine = true
  Ruled = false
  Sections = -> [Sketch016]
FEATURE [PartDesign::AdditiveLoft] AdditiveLoft002  label="loft_front"
  BaseFeature = -> AdditiveLoft001
  Closed = true
  Profile = -> Sketch029
  Refine = true
  Ruled = false
  Sections = -> [Sketch011]
FEATURE [PartDesign::Pad] Pad010  label="pad_flap_counter_right"
  BaseFeature = -> AdditiveLoft002
  Direction = (0,0,1)
  Length = 5
  Length2 = 10
  Profile = -> Sketch030
  Refine = true
  Type = 0
FEATURE [PartDesign::Pad] Pad011  label="pad_flap_counter_left"
  BaseFeature = -> Pad010
  Direction = (0,0,1)
  Length = 5
  Length2 = 10
  Profile = -> Sketch031
  Refine = true
  Reversed = true
  Type = 0
FEATURE [PartDesign::Pocket] Pocket003010  label="pocket_valve_top_connect_holes"
  BaseFeature = -> Pad011
  Direction = (0,1,2e-16)
  Length = 6
  Length2 = 100
  Profile = -> Sketch033
  Type = 0
FEATURE [PartDesign::Pocket] Pocket003011  label="pocket_valve_bottom_connect_holes"
  BaseFeature = -> Pocket003010
  Direction = (0,1,2e-16)
  Length = 6
  Length2 = 100
  Profile = -> Sketch034
  Reversed = true
  Type = 0
FEATURE [Sketcher::SketchObject] Sketch035  label="sk_flap_rod_counter"
  AttachmentOffset = pos=(0,0,6) rot=(0,0,1;0rad)
  FullyConstrained = true
  MapMode = 5
  Placement = pos=(0,0,6) rot=(0,0,1;0rad)
  Support = -> [XY_Plane001]
  sketch-geometry (4):
    g0: ArcOfCircle CenterX=-4.82 CenterY=0 CenterZ=0 NormalX=0 NormalY=0 NormalZ=1 AngleXU=0 Radius=3.545 StartAngle=1.5708 EndAngle=4.71239
    g1: ArcOfCircle CenterX=4.82 CenterY=0 CenterZ=0 NormalX=0 NormalY=0 NormalZ=1 AngleXU=0 Radius=3.545 StartAngle=4.71239 EndAngle=7.85398
    g2: LineSegment StartX=-4.82 StartY=-3.545 StartZ=0 EndX=4.82 EndY=-3.545 EndZ=0
    g3: LineSegment StartX=4.82 StartY=3.545 StartZ=0 EndX=-4.82 EndY=3.545 EndZ=0
  constraints (9):
    c: Tangent(g0,g2) = -1.5708
    c: Tangent(g2,g1) = -1.5708
    c: Tangent(g1,g3) = -1.5708
    c: Tangent(g3,g0) = -1.5708
    c: Equal(g0,g1)
    c: PointOnObject(g1,g-1)
    c: Symmetric(g1,g0,g-2)
    c: DistanceX(g3,g3) = 9.64  'flap_rod_counter_length'
    c: Diameter(g0) = 7.09  'flap_rod_counter_diameter'
FEATURE [PartDesign::Pad] Pad014  label="pad_flap_rod_counter"
  BaseFeature = -> Mirrored001
  Direction = (0,0,1)
  Length = 4
  Length2 = 10
  Profile = -> Sketch035
  Refine = true
  Reversed = true
  Type = 0
FEATURE [PartDesign::Pocket] Pocket003012  label="pocket_flap_rod_hole_through"
  BaseFeature = -> Pad014
  Direction = (-1,2e-16,-3e-16)
  Length = 5
  Length2 = 5
  Profile = -> Sketch006
  Refine = true
  Type = 1
FEATURE [Sketcher::SketchObject] Sketch036  label="sk_flap_rod_counter_hole"
  AttachmentOffset = pos=(0,0,6) rot=(0,0,1;0rad)
  FullyConstrained = true
  MapMode = 5
  Placement = pos=(0,0,6) rot=(0,0,1;0rad)
  Support = -> [XY_Plane001]
  expr: Constraints[1] = Spreadsheet.m2_inlay_width
  expr: Constraints[2] = <<Spreadsheet>>.flap_rod_counter_hole_center_distance * -1
  sketch-geometry (1):
    g0: Circle CenterX=-3.79 CenterY=0 CenterZ=0 NormalX=0 NormalY=0 NormalZ=1 AngleXU=0 Radius=1.7
  constraints (3):
    c: PointOnObject(g0,g-1)
    c: Diameter(g0) = 3.4
    c: DistanceX(g0) = -3.79
FEATURE [PartDesign::Pocket] Pocket003013  label="pocket_flap_rod_counter_hole"
  BaseFeature = -> Pocket003012
  Direction = (0,0,-1)
  Length = 5
  Length2 = 5
  Profile = -> Sketch036
  Refine = true
  Type = 0
FEATURE [PartDesign::Mirrored] Mirrored002
  BaseFeature = -> Pocket003013
  MirrorPlane = -> Sketch036 [V_Axis]
  Originals = -> [Pocket003013]
  Refine = true
FEATURE [PartDesign::Body] Body001  label="Flap"
  Group = -> [Sketch004,Pad002,Sketch005,Pad003,Sketch006,Sketch007,Pad004,Sketch008,Mirrored,Pocket,Mirrored001,Sketch035,Pad014,Pocket003012,Sketch036,Pocket003013,Mirrored002]
  Origin = -> Origin001
  Placement = pos=(0,0,23) rot=(0,0,1;1.5708rad)
  Tip = -> Mirrored002
FEATURE [Sketcher::SketchObject] Sketch037  label="sk_valve_back_extension"
  AttachmentOffset = pos=(0,0,-25) rot=(0,0,1;0rad)
  FullyConstrained = true
  MapMode = 5
  Placement = pos=(0,0,-25) rot=(0,0,1;0rad)
  Support = -> [XY_Plane002]
  expr: Constraints[2] = <<sk_fanduct_base>>.Constraints.duct_hole_diameter
  expr: Constraints[3] = <<sk_pipe>>.Constraints.pipe_outer_diameter
  sketch-geometry (2):
    g0: Circle CenterX=0 CenterY=0 CenterZ=0 NormalX=0 NormalY=0 NormalZ=1 AngleXU=0 Radius=38.15
    g1: Circle CenterX=0 CenterY=0 CenterZ=0 NormalX=0 NormalY=0 NormalZ=1 AngleXU=0 Radius=40.15
  constraints (4):
    c: Coincident(g0,g-1)
    c: Coincident(g1,g0)
    c: Diameter(g0) = 76.3
    c: Diameter(g1) = 80.3
FEATURE [PartDesign::Pad] Pad015  label="pad_valve_back_extension"
  BaseFeature = -> Pocket003011
  Direction = (0,0,1)
  Length = 20
  Length2 = 10
  Profile = -> Sketch037
  Refine = true
  Reversed = true
  Type = 0
FEATURE [PartDesign::Body] Body002  label="Valve"
  Group = -> [Sketch009,Pad005,Sketch011,Sketch012,Sketch014,Pocket003003,Pocket003004,Sketch015,Pocket003005,Sketch016,Sketch028,AdditiveLoft001,Sketch029,AdditiveLoft002,Sketch030,Pad010,Sketch031,Pad011,Sketch033,Pocket003010,Sketch034,Pocket003011,Sketch037,Pad015]
  Origin = -> Origin002
  Tip = -> Pad015
FEATURE [Sketcher::SketchObject] Sketch038  label="sk_cover_base"
  FullyConstrained = false
  MapMode = 5
  Support = -> [XY_Plane005]
  sketch-geometry (20):
    g0: Circle CenterX=0 CenterY=0 CenterZ=0 NormalX=0 NormalY=0 NormalZ=1 AngleXU=0 Radius=51.3665
    g1: ArcOfCircle CenterX=0 CenterY=0 CenterZ=0 NormalX=0 NormalY=0 NormalZ=1 AngleXU=0 Radius=48.3889 StartAngle=4.74317 EndAngle=6.2524
    g2: LineSegment StartX=1.48945 StartY=48.366 StartZ=0 EndX=1.48945 EndY=8 EndZ=0
    g3: LineSegment StartX=-1.48945 StartY=-48.366 StartZ=0 EndX=-1.48945 EndY=-8 EndZ=0
    g4: ArcOfCircle CenterX=0 CenterY=0 CenterZ=0 NormalX=0 NormalY=0 NormalZ=1 AngleXU=0 Radius=48.3889 StartAngle=1.60158 EndAngle=3.11081
    g5: LineSegment StartX=-48.366 StartY=1.48945 StartZ=0 EndX=-8 EndY=1.48945 EndZ=0
    g6: LineSegment StartX=48.366 StartY=-1.48945 StartZ=0 EndX=8 EndY=-1.48945 EndZ=0
    g7: ArcOfCircle CenterX=0 CenterY=0 CenterZ=0 NormalX=0 NormalY=0 NormalZ=1 AngleXU=0 Radius=48.3889 StartAngle=3.17238 EndAngle=4.6816
    g8: ArcOfCircle CenterX=0 CenterY=0 CenterZ=0 NormalX=0 NormalY=0 NormalZ=1 AngleXU=0 Radius=48.3889 StartAngle=0.0307857 EndAngle=1.54001
    g9: LineSegment StartX=8 StartY=1.48945 StartZ=0 EndX=48.366 EndY=1.48945 EndZ=0
    g10: LineSegment StartX=-8 StartY=-1.48945 StartZ=0 EndX=-48.366 EndY=-1.48945 EndZ=0
    g11: LineSegment StartX=-1.48945 StartY=8 StartZ=0 EndX=-1.48945 EndY=48.366 EndZ=0
    g12: LineSegment StartX=1.48945 StartY=-8 StartZ=0 EndX=1.48945 EndY=-48.366 EndZ=0
    g13: LineSegment StartX=48.366 StartY=-1.48945 StartZ=0 EndX=48.366 EndY=1.48945 EndZ=0
    g14: LineSegment StartX=-1.48945 StartY=48.366 StartZ=0 EndX=1.48945 EndY=48.366 EndZ=0
    g15: LineSegment StartX=48.366 StartY=-1.48945 StartZ=0 EndX=51.3449 EndY=-1.48945 EndZ=0
    g16: ArcOfCircle CenterX=0 CenterY=0 CenterZ=0 NormalX=0 NormalY=0 NormalZ=1 AngleXU=0 Radius=8.13747 StartAngle=3.32567 EndAngle=4.52831
    g17: ArcOfCircle CenterX=0 CenterY=0 CenterZ=0 NormalX=0 NormalY=0 NormalZ=1 AngleXU=0 Radius=8.13747 StartAngle=0.184074 EndAngle=1.38672
    g18: ArcOfCircle CenterX=0 CenterY=0 CenterZ=0 NormalX=0 NormalY=0 NormalZ=1 AngleXU=0 Radius=8.13747 StartAngle=1.75487 EndAngle=2.95752
    g19: ArcOfCircle CenterX=0 CenterY=0 CenterZ=0 NormalX=0 NormalY=0 NormalZ=1 AngleXU=0 Radius=8.13747 StartAngle=4.89646 EndAngle=6.09911
  constraints (54):
    c: Coincident(g0,g-1)
    c: Coincident(g1,g0)
    c: Vertical(g2)
    c: Symmetric(g2,g11,g-2)
    c: Coincident(g7,g3)
    c: Coincident(g1,g12)
    c: PointOnObject(g8,g2)
    c: Coincident(g4,g11)
    c: Coincident(g1,g4)
    c: Horizontal(g5)
    c: Coincident(g4,g5)
    c: Coincident(g7,g10)
    c: Coincident(g4,g7)
    c: Equal(g1,g8)
    c: Coincident(g1,g6)
    c: PointOnObject(g8,g5)
    c: Coincident(g1,g8)
    c: Symmetric(g7,g1,g-2)
    c: Coincident(g9,g8)
    c: Symmetric(g7,g4,g-1)
    c: Vertical(g12)
    c: Vertical(g3)
    c: Coincident(g13,g1)
    c: Coincident(g13,g8)
    c: Coincident(g14,g4)
    c: Coincident(g14,g2)
    c: Equal(g14,g13)
    c: Coincident(g15,g1)
    c: PointOnObject(g15,g0)
    c: Horizontal(g15)
    c: Equal(g15,g13)
    c: Coincident(g16,g0)
    c: PointOnObject(g2,g16)
    c: Symmetric(g12,g3,g-2)
    c: Coincident(g18,g5)
    c: Coincident(g16,g10)
    c: Equal(g16,g17)
    c: Coincident(g19,g6)
    c: Coincident(g17,g9)
    c: Coincident(g16,g17)
    c: Equal(g17,g18)
    c: PointOnObject(g17,g2)
    c: PointOnObject(g18,g11)
    c: Coincident(g17,g18)
    c: Equal(g16,g19)
    c: Coincident(g16,g3)
    c: PointOnObject(g19,g12)
    c: Coincident(g16,g19)
    c: Horizontal(g9)
    c: Horizontal(g6)
    c: Horizontal(g10)
    c: Vertical(g11)
    c: Symmetric(g11,g3,g-1)
    c: DistanceX(g5,g0) = 8  'inner_radius'
FEATURE [PartDesign::Pad] Pad016
  Direction = (0,0,1)
  Length = 10
  Length2 = 10
  Profile = -> Sketch038
  Refine = true
  Type = 0
FEATURE [Sketcher::SketchObject] Sketch039
  AttachmentOffset = pos=(0,10,0) rot=(0,0,1;0rad)
  FullyConstrained = false
  MapMode = 5
  Placement = pos=(-2.2e-15,2.2e-15,10) rot=(0.57735,0.57735,0.57735;2.0944rad)
  Support = -> [YZ_Plane005]
  expr: .AttachmentOffset.Base.y = <<Pad016>>.Length
  expr: Constraints[11] = <<sk_cover_base>>.Constraints.inner_radius
  sketch-geometry (7):
    g0: ArcOfEllipse CenterX=0 CenterY=0 CenterZ=0 NormalX=0 NormalY=0 NormalZ=1 MajorRadius=17.0191 MinorRadius=8 AngleXU=1.5708 StartAngle=0 EndAngle=1.5708
    g1: LineSegment StartX=0 StartY=17.0191 StartZ=0 EndX=0 EndY=-17.0191 EndZ=0
    g2: LineSegment StartX=-8 StartY=0 StartZ=0 EndX=8 EndY=0 EndZ=0
    g3: GeomPoint X=0 Y=15.0217 Z=0
    g4: GeomPoint X=0 Y=-15.0217 Z=0
    g5: LineSegment StartX=-8 StartY=0 StartZ=0 EndX=0 EndY=0 EndZ=0
    g6: LineSegment StartX=0 StartY=0 StartZ=0 EndX=0 EndY=17.0191 EndZ=0
  constraints (10):
    c: InternalAlignment(g1-g4 -> g0) x4
    c: Vertical(g1)
    c: Coincident(g5,g2)
    c: Coincident(g5,g0)
    c: Coincident(g6,g0)
    c: Coincident(g6,g1)
    c: PointOnObject(g0,g2)
    c: Coincident(g0,g-1)
    c: DistanceX(g5,g5) = 8
    c: Coincident(g0,g6)
FEATURE [PartDesign::Revolution] Revolution
  Angle = 360
  Axis = (-2e-16,3e-16,1)
  Base = (-2.2e-15,2.2e-15,10)
  BaseFeature = -> Pad016
  Profile = -> Sketch039
  ReferenceAxis = -> Sketch039 [V_Axis]
  Refine = true
FEATURE [PartDesign::Body] Body005
  Group = -> [Sketch038,Pad016,Sketch039,Revolution]
  Origin = -> Origin005
  Placement = pos=(0,0,168) rot=(0,0,1;0rad)
  Tip = -> Revolution
FEATURE [Sketcher::SketchObject] Sketch040  label="sk_servo_hold_base"
  FullyConstrained = false
  MapMode = 5
  Support = -> [XY_Plane006]
  expr: Constraints[16] = <<sk_valve_base>>.Constraints.top_angle
  expr: Constraints[8] = <<sk_valve_base>>.Constraints.top_angle
  expr: Constraints[9] = <<sk_valve_base>>.Constraints.top_width + 0.5mm
  sketch-geometry (8):
    g0: LineSegment StartX=-20.8463 StartY=70.7352 StartZ=0 EndX=20.8463 EndY=70.7352 EndZ=0
    g1: LineSegment StartX=17.75 StartY=51.0887 StartZ=0 EndX=-17.75 EndY=51.0887 EndZ=0
    g2: LineSegment StartX=-24.2526 StartY=64.8332 StartZ=0 EndX=-24.2526 EndY=39.8217 EndZ=0
    g3: LineSegment StartX=-24.2526 StartY=39.8217 StartZ=0 EndX=-17.75 EndY=51.0887 EndZ=0
    g4: LineSegment StartX=17.75 StartY=51.0887 StartZ=0 EndX=24.2526 EndY=39.8217 EndZ=0
    g5: LineSegment StartX=24.2526 StartY=39.8217 StartZ=0 EndX=24.2526 EndY=64.8332 EndZ=0
    g6: LineSegment StartX=-24.2526 StartY=64.8332 StartZ=0 EndX=-20.8463 EndY=70.7352 EndZ=0
    g7: LineSegment StartX=20.8463 StartY=70.7352 StartZ=0 EndX=24.2526 EndY=64.8332 EndZ=0
  constraints (17):
    c: Horizontal(g1)
    c: Vertical(g2)
    c: Coincident(g3,g2)
    c: Coincident(g5,g4)
    c: Symmetric(g3,g4,g-2)
    c: Symmetric(g2,g4,g-2)
    c: Coincident(g1,g3)
    c: PointOnObject(g1,g4)
    c: Angle(g3,g1) = 2.09424
    c: DistanceX(g1,g1) = 35.5
    c: Coincident(g0,g6)
    c: Coincident(g2,g6)
    c: Coincident(g0,g7)
    c: Coincident(g5,g7)
    c: Symmetric(g0,g0,g-2)
    c: Symmetric(g2,g5,g-2)
    c: Angle(g6,g0) = 2.09424
FEATURE [PartDesign::Pad] Pad017  label="pad_servo_hold_base"
  Direction = (0,0,1)
  Length = 40
  Length2 = 10
  Profile = -> Sketch040
  Refine = true
  Type = 0
FEATURE [Sketcher::SketchObject] Sketch042  label="sk_servo_hold_front_cutout"
  AttachmentOffset = pos=(0,0,40) rot=(0,0,1;0rad)
  FullyConstrained = false
  MapMode = 5
  Placement = pos=(0,0,40) rot=(0,0,1;0rad)
  Support = -> [XY_Plane006]
  expr: Constraints[11] = <<sk_valve_base>>.Constraints.top_angle
  sketch-geometry (6):
    g0: LineSegment StartX=-16.0364 StartY=67.7723 StartZ=0 EndX=16.0364 EndY=67.7723 EndZ=0
    g1: LineSegment StartX=18.7646 StartY=63.0453 StartZ=0 EndX=18.7646 EndY=55.1714 EndZ=0
    g2: LineSegment StartX=18.7646 StartY=55.1714 StartZ=0 EndX=-18.7646 EndY=55.1714 EndZ=0
    g3: LineSegment StartX=-18.7646 StartY=55.1714 StartZ=0 EndX=-18.7646 EndY=63.0453 EndZ=0
    g4: LineSegment StartX=-18.7646 StartY=63.0453 StartZ=0 EndX=-16.0364 EndY=67.7723 EndZ=0
    g5: LineSegment StartX=16.0364 StartY=67.7723 StartZ=0 EndX=18.7646 EndY=63.0453 EndZ=0
  constraints (12):
    c: Coincident(g1,g2)
    c: Coincident(g2,g3)
    c: Horizontal(g2)
    c: Vertical(g1)
    c: Vertical(g3)
    c: Coincident(g0,g4)
    c: Coincident(g3,g4)
    c: Coincident(g0,g5)
    c: Coincident(g1,g5)
    c: Symmetric(g0,g0,g-2)
    c: Symmetric(g3,g1,g-2)
    c: Angle(g4,g0) = 2.09424
FEATURE [Sketcher::SketchObject] Sketch043  label="sk_servo_hold_side_cutout"
  AttachmentOffset = pos=(0,0,25) rot=(0,0,1;0rad)
  FullyConstrained = false
  MapMode = 5
  Placement = pos=(25,-5.6e-15,5.6e-15) rot=(0.57735,0.57735,0.57735;2.0944rad)
  Support = -> [YZ_Plane006]
  sketch-geometry (4):
    g0: LineSegment StartX=65.944 StartY=37.2637 StartZ=0 EndX=56.8668 EndY=37.2637 EndZ=0
    g1: LineSegment StartX=56.8668 StartY=37.2637 StartZ=0 EndX=56.8668 EndY=3.01771 EndZ=0
    g2: LineSegment StartX=56.8668 StartY=3.01771 StartZ=0 EndX=65.944 EndY=3.01771 EndZ=0
    g3: LineSegment StartX=65.944 StartY=3.01771 StartZ=0 EndX=65.944 EndY=37.2637 EndZ=0
  constraints (8):
    c: Coincident(g0,g1)
    c: Coincident(g1,g2)
    c: Coincident(g2,g3)
    c: Coincident(g3,g0)
    c: Horizontal(g0)
    c: Horizontal(g2)
    c: Vertical(g1)
    c: Vertical(g3)
FEATURE [Sketcher::SketchObject] Sketch045  label="sk_valve_front_taper001"
  AttachmentOffset = pos=(0,0,80) rot=(0,0,1;0rad)
  FullyConstrained = true
  MapMode = 5
  Placement = pos=(0,0,80) rot=(0,0,1;0rad)
  Support = -> [XY_Plane007]
  expr: .AttachmentOffset.Base.z = <<pad_valve_base>>.Length + 40mm
  expr: Constraints[2] = <<sk_fanduct_base>>.Constraints.duct_hole_diameter - 2mm
  expr: Constraints[3] = <<sk_pipe>>.Constraints.pipe_outer_diameter + 20mm
  sketch-geometry (2):
    g0: Circle CenterX=0 CenterY=0 CenterZ=0 NormalX=0 NormalY=0 NormalZ=1 AngleXU=0 Radius=37.15
    g1: Circle CenterX=0 CenterY=0 CenterZ=0 NormalX=0 NormalY=0 NormalZ=1 AngleXU=0 Radius=50.15
  constraints (4):
    c: Coincident(g0,g-1)
    c: Coincident(g1,g0)
    c: Diameter(g0) = 74.3
    c: Diameter(g1) = 100.3
FEATURE [Sketcher::SketchObject] Sketch046  label="sk_valve_front_taper002"
  AttachmentOffset = pos=(0,0,80) rot=(0,0,1;0rad)
  FullyConstrained = true
  MapMode = 5
  Placement = pos=(0,0,80) rot=(0,0,1;0rad)
  Support = -> [XY_Plane007]
  expr: .AttachmentOffset.Base.z = <<pad_valve_base>>.Length + 40mm
  expr: Constraints[2] = <<sk_fanduct_base>>.Constraints.duct_hole_diameter
  expr: Constraints[3] = <<sk_pipe>>.Constraints.pipe_outer_diameter + 18mm
  sketch-geometry (2):
    g0: Circle CenterX=0 CenterY=0 CenterZ=0 NormalX=0 NormalY=0 NormalZ=1 AngleXU=0 Radius=38.15
    g1: Circle CenterX=0 CenterY=0 CenterZ=0 NormalX=0 NormalY=0 NormalZ=1 AngleXU=0 Radius=49.15
  constraints (4):
    c: Coincident(g0,g-1)
    c: Coincident(g1,g0)
    c: Diameter(g0) = 76.3
    c: Diameter(g1) = 98.3
FEATURE [Sketcher::SketchObject] Sketch047
  FullyConstrained = true
  MapMode = 5
  Support = -> [XY_Plane008]
  sketch-geometry (2):
    g0: Circle CenterX=0 CenterY=0 CenterZ=0 NormalX=0 NormalY=0 NormalZ=1 AngleXU=0 Radius=39
    g1: Circle CenterX=0 CenterY=0 CenterZ=0 NormalX=0 NormalY=0 NormalZ=1 AngleXU=0 Radius=48
  constraints (4):
    c: Coincident(g0,g-1)
    c: Diameter(g0) = 78
    c: Coincident(g1,g0)
    c: Diameter(g1) = 96
FEATURE [PartDesign::Pad] Pad019
  Direction = (0,0,1)
  Length = 4.9
  Length2 = 10
  Profile = -> Sketch047
  Refine = true
  Type = 0
FEATURE [PartDesign::Body] Body008  label="led_ring"
  Group = -> [Sketch047,Pad019]
  Origin = -> Origin008
  Placement = pos=(0,0,88) rot=(0,0,1;0rad)
  Tip = -> Pad019
FEATURE [Sketcher::SketchObject] Sketch048
  AttachmentOffset = pos=(0,0,100) rot=(0,0,1;0rad)
  FullyConstrained = true
  MapMode = 5
  Placement = pos=(0,0,100) rot=(0,0,1;0rad)
  Support = -> [XY_Plane007]
  sketch-geometry (2):
    g0: Circle CenterX=0 CenterY=0 CenterZ=0 NormalX=0 NormalY=0 NormalZ=1 AngleXU=0 Radius=39
    g1: Circle CenterX=0 CenterY=0 CenterZ=0 NormalX=0 NormalY=0 NormalZ=1 AngleXU=0 Radius=48
  constraints (4):
    c: Coincident(g0,g-1)
    c: Diameter(g0) = 78
    c: Coincident(g1,g0)
    c: Diameter(g1) = 96
FEATURE [Sketcher::SketchObject] Sketch050  label="sk_servo_hold_top_holes"
  AttachmentOffset = pos=(0,0,-71) rot=(0,0,1;0rad)
  FullyConstrained = true
  MapMode = 5
  Placement = pos=(0,71,1.58e-14) rot=(1,0,0;1.5708rad)
  Support = -> [XZ_Plane006]
  expr: Constraints[2] = <<Spreadsheet>>.m3_inlay_width
  expr: Constraints[3] = <<sk_valve_top_connect_holes>>.Constraints.rear_distance
  expr: Constraints[4] = <<sk_valve_top_connect_holes>>.Constraints.center_distance
  sketch-geometry (2):
    g0: Circle CenterX=-13.83 CenterY=19.55 CenterZ=0 NormalX=0 NormalY=0 NormalZ=1 AngleXU=0 Radius=2.24
    g1: Circle CenterX=13.83 CenterY=19.55 CenterZ=0 NormalX=0 NormalY=0 NormalZ=1 AngleXU=0 Radius=2.24
  constraints (5):
    c: Symmetric(g0,g1,g-2)
    c: Equal(g0,g1)
    c: Diameter(g0) = 4.48
    c: DistanceY(g-1,g0) = 19.55
    c: DistanceX(g0,g-1) = 13.83
FEATURE [Sketcher::SketchObject] Sketch053
  AttachmentOffset = pos=(0,0,80) rot=(0,0,1;0rad)
  ExternalGeometry = -> [Sketch045]
  FullyConstrained = false
  MapMode = 5
  Placement = pos=(0,0,80) rot=(0,0,1;0rad)
  Support = -> [XY_Plane007]
  sketch-geometry (14):
    g0: ArcOfCircle CenterX=-8e-15 CenterY=-4.97e-14 CenterZ=0 NormalX=0 NormalY=0 NormalZ=1 AngleXU=0 Radius=50.15 StartAngle=1.45867 EndAngle=1.5708
    g1: ArcOfCircle CenterX=-8e-15 CenterY=-4.97e-14 CenterZ=0 NormalX=0 NormalY=0 NormalZ=1 AngleXU=0 Radius=49.15 StartAngle=1.47904 EndAngle=1.5708
    g2: LineSegment StartX=5.61117 StartY=49.8351 StartZ=0 EndX=5.49928 EndY=48.8414 EndZ=0
    g3: ArcOfCircle CenterX=-8e-15 CenterY=-4.97e-14 CenterZ=0 NormalX=0 NormalY=0 NormalZ=1 AngleXU=0 Radius=50.15 StartAngle=1.5708 EndAngle=1.68292
    g4: ArcOfCircle CenterX=-8e-15 CenterY=-4.97e-14 CenterZ=0 NormalX=0 NormalY=0 NormalZ=1 AngleXU=0 Radius=49.15 StartAngle=1.5708 EndAngle=1.66255
    g5: LineSegment StartX=-5.49928 StartY=48.8414 StartZ=0 EndX=-5.61117 EndY=49.8351 EndZ=0
    g6: LineSegment StartX=-8e-15 StartY=-4.97e-14 StartZ=0 EndX=5.61117 EndY=49.8351 EndZ=0
    g7: LineSegment StartX=5.49928 StartY=48.8414 StartZ=0 EndX=4.15663 EndY=36.9167 EndZ=0
    g8: LineSegment StartX=-5.49928 StartY=48.8414 StartZ=0 EndX=-4.15663 EndY=36.9167 EndZ=0
    g9: LineSegment StartX=-4.50335 StartY=48.9433 StartZ=0 EndX=-3.23887 EndY=37.7128 EndZ=0
    g10: LineSegment StartX=4.50335 StartY=48.9433 StartZ=0 EndX=3.23887 EndY=37.7128 EndZ=0
    g11: ArcOfCircle CenterX=-8e-15 CenterY=-4.97e-14 CenterZ=0 NormalX=0 NormalY=0 NormalZ=1 AngleXU=0 Radius=37.8516 StartAngle=1.48512 EndAngle=1.65647
    g12: ArcOfCircle CenterX=-8e-15 CenterY=-4.97e-14 CenterZ=0 NormalX=0 NormalY=0 NormalZ=1 AngleXU=0 Radius=37.15 StartAngle=1.45867 EndAngle=1.68292
    g13: LineSegment StartX=-5.61117 StartY=49.8351 StartZ=0 EndX=-8e-15 EndY=-4.97e-14 EndZ=0
  constraints (39):
    c: PointOnObject(g0,g-2)
    c: PointOnObject(g0,g-3)
    c: Coincident(g1,g0)
    c: Coincident(g2,g0)
    c: Coincident(g3,g0)
    c: Coincident(g4,g0)
    c: Coincident(g5,g3)
    c: Distance(g2) = 1
    c: Coincident(g6,g0)
    c: Coincident(g6,g0)
    c: Coincident(g0,g3)
    c: Coincident(g4,g1)
    c: PointOnObject(g2,g6)
    c: Distance(g0,g0) = 5.62
    c: Distance(g0,g3) = 5.62
    c: PointOnObject(g0,g-3)
    c: PointOnObject(g1,g-2)
    c: Coincident(g7,g2)
    c: PointOnObject(g7,g6)
    c: PointOnObject(g7,g-4)
    c: Coincident(g8,g5)
    c: PointOnObject(g8,g-4)
    c: Symmetric(g9,g10,g-2)
    c: Coincident(g11,g0)
    c: Coincident(g4,g9)
    c: PointOnObject(g1,g10)
    c: Coincident(g10,g11)
    c: Coincident(g9,g11)
    c: Parallel(g10,g7)
    c: Coincident(g12,g0)
    c: Coincident(g12,g8)
    c: Coincident(g12,g7)
    c: Parallel(g8,g9)
    c: PointOnObject(g5,g4)
    c: Equal(g5,g2)
    c: Coincident(g13,g3)
    c: Coincident(g13,g0)
    c: PointOnObject(g8,g13)
    c: PointOnObject(g5,g13)
FEATURE [PartDesign::Pad] Pad021
  Direction = (0,0,1)
  Length = 10
  Length2 = 10
  Profile = -> Sketch053
  Refine = true
  Reversed = true
  Type = 0
FEATURE [PartDesign::PolarPattern] PolarPattern
  Angle = 360
  Axis = -> Sketch053 [N_Axis]
  BaseFeature = -> Pad021
  Occurrences = 3
  Originals = -> [Pad021]
  Refine = true
FEATURE [PartDesign::Pocket] Pocket003020
  BaseFeature = -> PolarPattern
  Direction = (0,0,-1)
  Length = 5
  Length2 = 5
  Profile = -> Sketch046
  Refine = true
  Type = 0
FEATURE [PartDesign::Body] Body007
  Group = -> [Sketch045,Sketch046,Sketch048,Sketch053,Pad021,PolarPattern,Pocket003020]
  Origin = -> Origin007
  Placement = pos=(0,0,243) rot=(0,1,0;3.14159rad)
  Tip = -> Pocket003020
FEATURE [Sketcher::SketchObject] Sketch054  label="sk_valve_front_taper003"
  AttachmentOffset = pos=(0,0,80) rot=(0,0,1;0rad)
  FullyConstrained = true
  MapMode = 5
  Placement = pos=(0,0,80) rot=(0,0,1;0rad)
  Support = -> [XY_Plane009]
  expr: .AttachmentOffset.Base.z = <<pad_valve_base>>.Length + 40mm
  expr: Constraints[2] = <<sk_fanduct_base>>.Constraints.duct_hole_diameter - 2mm
  expr: Constraints[3] = <<sk_pipe>>.Constraints.pipe_outer_diameter + 20mm
  sketch-geometry (2):
    g0: Circle CenterX=0 CenterY=0 CenterZ=0 NormalX=0 NormalY=0 NormalZ=1 AngleXU=0 Radius=37.15
    g1: Circle CenterX=0 CenterY=0 CenterZ=0 NormalX=0 NormalY=0 NormalZ=1 AngleXU=0 Radius=50.15
  constraints (4):
    c: Coincident(g0,g-1)
    c: Coincident(g1,g0)
    c: Diameter(g0) = 74.3
    c: Diameter(g1) = 100.3
FEATURE [PartDesign::Pad] Pad022
  Direction = (0,0,1)
  Length = 2
  Length2 = 10
  Profile = -> Sketch054
  Refine = true
  Type = 0
FEATURE [PartDesign::Body] Body009
  Group = -> [Sketch054,Pad022]
  Origin = -> Origin009
  Placement = pos=(0,0,280) rot=(0,1,0;3.14159rad)
  Tip = -> Pad022
FEATURE [Sketcher::SketchObject] Sketch055  label="sk_valve_front_taper004"
  AttachmentOffset = pos=(0,0,80) rot=(0,0,1;0rad)
  FullyConstrained = true
  MapMode = 5
  Placement = pos=(0,0,80) rot=(0,0,1;0rad)
  Support = -> [XY_Plane010]
  expr: .AttachmentOffset.Base.z = <<pad_valve_base>>.Length + 40mm
  expr: Constraints[2] = <<sk_fanduct_base>>.Constraints.duct_hole_diameter - 2mm
  expr: Constraints[3] = <<sk_pipe>>.Constraints.pipe_outer_diameter + 25mm
  sketch-geometry (2):
    g0: Circle CenterX=0 CenterY=0 CenterZ=0 NormalX=0 NormalY=0 NormalZ=1 AngleXU=0 Radius=37.15
    g1: Circle CenterX=0 CenterY=0 CenterZ=0 NormalX=0 NormalY=0 NormalZ=1 AngleXU=0 Radius=52.65
  constraints (4):
    c: Coincident(g0,g-1)
    c: Coincident(g1,g0)
    c: Diameter(g0) = 74.3
    c: Diameter(g1) = 105.3
FEATURE [PartDesign::Pad] Pad023
  Direction = (0,0,1)
  Length = 25
  Length2 = 10
  Profile = -> Sketch055
  Refine = true
  Type = 0
FEATURE [Sketcher::SketchObject] Sketch056  label="sk_valve_front_taper005"
  AttachmentOffset = pos=(0,0,80) rot=(0,0,1;0rad)
  FullyConstrained = true
  MapMode = 5
  Placement = pos=(0,0,80) rot=(0,0,1;0rad)
  Support = -> [XY_Plane010]
  expr: .AttachmentOffset.Base.z = <<pad_valve_base>>.Length + 40mm
  expr: Constraints[2] = <<sk_fanduct_base>>.Constraints.duct_hole_diameter + 4mm
  expr: Constraints[3] = <<sk_pipe>>.Constraints.pipe_outer_diameter + 25mm
  sketch-geometry (2):
    g0: Circle CenterX=0 CenterY=0 CenterZ=0 NormalX=0 NormalY=0 NormalZ=1 AngleXU=0 Radius=40.15
    g1: Circle CenterX=0 CenterY=0 CenterZ=0 NormalX=0 NormalY=0 NormalZ=1 AngleXU=0 Radius=52.65
  constraints (4):
    c: Coincident(g0,g-1)
    c: Coincident(g1,g0)
    c: Diameter(g0) = 80.3
    c: Diameter(g1) = 105.3
FEATURE [PartDesign::Pocket] Pocket003021
  BaseFeature = -> Pad023
  Direction = (0,0,-1)
  Length = 10
  Length2 = 5
  Profile = -> Sketch056
  Refine = true
  Reversed = true
  Type = 0
FEATURE [Sketcher::SketchObject] Sketch057  label="sk_valve_front_taper006"
  AttachmentOffset = pos=(0,0,105) rot=(0,0,1;0rad)
  FullyConstrained = true
  MapMode = 5
  Placement = pos=(0,0,105) rot=(0,0,1;0rad)
  Support = -> [XY_Plane010]
  expr: Constraints[2] = <<sk_fanduct_base>>.Constraints.duct_hole_diameter + 2mm
  expr: Constraints[3] = <<sk_pipe>>.Constraints.pipe_outer_diameter + 23mm
  sketch-geometry (2):
    g0: Circle CenterX=0 CenterY=0 CenterZ=0 NormalX=0 NormalY=0 NormalZ=1 AngleXU=0 Radius=39.15
    g1: Circle CenterX=0 CenterY=0 CenterZ=0 NormalX=0 NormalY=0 NormalZ=1 AngleXU=0 Radius=51.65
  constraints (4):
    c: Coincident(g0,g-1)
    c: Coincident(g1,g0)
    c: Diameter(g0) = 78.3
    c: Diameter(g1) = 103.3
FEATURE [PartDesign::Pocket] Pocket003022
  BaseFeature = -> Pocket003021
  Direction = (0,0,-1)
  Length = 13
  Length2 = 5
  Profile = -> Sketch057
  Refine = true
  Type = 0
FEATURE [Sketcher::SketchObject] Sketch058
  FullyConstrained = false
  MapMode = 5
  Placement = pos=(0,0,0) rot=(0.57735,0.57735,0.57735;2.0944rad)
  Support = -> [YZ_Plane011]
  sketch-geometry (5):
    g0: ArcOfCircle CenterX=-42.7782 CenterY=168.893 CenterZ=0 NormalX=0 NormalY=0 NormalZ=1 AngleXU=0 Radius=8.5228 StartAngle=0.546997 EndAngle=2.5946
    g1: LineSegment StartX=-50.0575 StartY=173.326 StartZ=0 EndX=-35.499 EndY=173.326 EndZ=0
    g2: ArcOfCircle CenterX=-42.7782 CenterY=168.651 CenterZ=0 NormalX=0 NormalY=0 NormalZ=1 AngleXU=0 Radius=8.10741 StartAngle=0.614615 EndAngle=2.52698
    g3: LineSegment StartX=-50.0575 StartY=173.326 StartZ=0 EndX=-49.402 EndY=173.326 EndZ=0
    g4: LineSegment StartX=-36.1545 StartY=173.326 StartZ=0 EndX=-35.499 EndY=173.326 EndZ=0
  constraints (10):
    c: Coincident(g1,g0)
    c: Coincident(g1,g0)
    c: Horizontal(g1)
    c: PointOnObject(g2,g1)
    c: PointOnObject(g2,g1)
    c: Coincident(g3,g0)
    c: Coincident(g3,g2)
    c: Coincident(g4,g2)
    c: Coincident(g4,g0)
    c: Equal(g4,g3)
FEATURE [PartDesign::Revolution] Revolution001
  Angle = 360
  Axis = (-2e-16,3e-16,1)
  Base = (0,0,0)
  Placement = pos=(0,0,0) rot=(0.57735,0.57735,0.57735;2.0944rad)
  Profile = -> Sketch058
  ReferenceAxis = -> Sketch058 [V_Axis]
  Refine = true
FEATURE [PartDesign::Body] Body011
  Group = -> [Sketch058,Revolution001]
  Origin = -> Origin011
  Placement = pos=(0,0,15) rot=(0,0,1;0rad)
  Tip = -> Revolution001
FEATURE [PartDesign::Fillet] Fillet
  Base = -> Pocket003022 [Edge1]
  BaseFeature = -> Pocket003022
  Radius = 4
  Refine = true
  SupportTransform = false
  UseAllEdges = false
FEATURE [PartDesign::Body] Body010
  Group = -> [Sketch055,Pad023,Sketch056,Pocket003021,Sketch057,Pocket003022,Fillet]
  Origin = -> Origin010
  Placement = pos=(0,0,14) rot=(0,0,1;0rad)
  Tip = -> Fillet
FEATURE [Spreadsheet::Sheet] Spreadsheet
  cells = A1=duct_hole_diameter; B1(duct_hole_diameter)==<<sk_fanduct_base>>.Constraints.duct_hole_diameter; A2=pipe_outer_diameter; B2(pipe_outer_diameter)==<<sk_pipe>>.Constraints.pipe_outer_diameter; F2=m4_nut_depth; G2(m4_nut_depth)==3.2mm; A3=pipe_width; B3(pipe_width)==pipe_outer_diameter - duct_hole_diameter; F3=m4_nut_distance; G3(m4_nut_distance)==7.7mm; A4=flap_diameter; B4(flap_diameter)==duct_hole_diameter - 1mm; A5=flap_rod_hole_diameter; B5(flap_rod_hole_diameter)==3.5mm; A6=flap_rod_width; B6(flap_rod_width)==2mm; A7=flap_rod_nut_width; B7(flap_rod_nut_width)==6.1mm; A8=flap_rod_counter_diameter; B8(flap_rod_counter_diameter)==<<sk_flap_rod_counter>>.Constraints.flap_rod_counter_diameter; A9=flap_rod_counter_length; B9(flap_rod_counter_length)==<<sk_flap_rod_counter>>.Constraints.flap_rod_counter_length; A10=flap_rod_counter_hole_center_distance; B10(flap_rod_counter_hole_center_distance)==3.79mm; A11=flap_width; B11(flap_width)==2mm; A13=m2_inlay_width; B13(m2_inlay_width)==3.4mm; A14=m3_inlay_width; B14(m3_inlay_width)==4.48mm; A16=front_led_ring_inner_diameter; B16(front_led_ring_inner_diameter)==78mm; A17=front_led_ring_outer_diameter; B17(front_led_ring_outer_diameter)==96mm; A19=fan_duct_width; B19(fan_duct_width)==100mm; A20=fan_duct_depth; B20(fan_duct_depth)==45mm; A21=fan_mounting_hole_distance; B21(fan_mounting_hole_distance)==71.5mm; A22=fan_mounting_hole_diameter; B22(fan_mounting_hole_diameter)==4.3mm; A23=fan_mount_hole_screw_inlay; B23(fan_mount_hole_screw_inlay)==8mm; A24=fan_mount_width; B24(fan_mount_width)==100mm; A25=fan_mount_overhang; B25(fan_mount_overhang)==15mm; A26=fan_mount_depth; B26(fan_mount_depth)==50mm; A28=fan_depth; B28(fan_depth)==35mm; A31=fan_mount_outer_radius; B31(fan_mount_outer_radius)==fan_mount_width / sqrt(2)
FEATURE [App::DocumentObjectGroup] Group  label="Gruppe"
  Group = -> [Body007,Body008,Body009,Body010,Body011,Body005]
FEATURE [App::DocumentObjectGroup] Group001  label="_"
  Group = -> [Pocket003001,Pocket003002,Part__Feature]
FEATURE [Sketcher::SketchObject] Sketch060  label="sk_servo_clip_mount_holes"
  AttachmentOffset = pos=(0,0,-74) rot=(0,0,1;0rad)
  FullyConstrained = true
  MapMode = 5
  Placement = pos=(0,74,1.64e-14) rot=(1,0,0;1.5708rad)
  Support = -> [XZ_Plane012]
  expr: Constraints[3] = <<sk_valve_top_connect_holes>>.Constraints.rear_distance
  expr: Constraints[4] = <<sk_valve_top_connect_holes>>.Constraints.center_distance
  sketch-geometry (2):
    g0: Circle CenterX=-13.83 CenterY=19.55 CenterZ=0 NormalX=0 NormalY=0 NormalZ=1 AngleXU=0 Radius=1.6
    g1: Circle CenterX=13.83 CenterY=19.55 CenterZ=0 NormalX=0 NormalY=0 NormalZ=1 AngleXU=0 Radius=1.6
  constraints (5):
    c: Symmetric(g0,g1,g-2)
    c: Equal(g0,g1)
    c: Diameter(g0) = 3.2
    c: DistanceY(g-1,g0) = 19.55
    c: DistanceX(g0,g-1) = 13.83
FEATURE [Sketcher::SketchObject] Sketch061  label="sk_servo_clip_base"
  AttachmentOffset = pos=(0,0,19.55) rot=(0,0,1;0rad)
  FullyConstrained = false
  MapMode = 5
  Placement = pos=(0,0,19.55) rot=(0,0,1;0rad)
  Support = -> [XY_Plane012]
  expr: .AttachmentOffset.Base.z = <<sk_valve_top_connect_holes>>.Constraints.rear_distance
  sketch-geometry (16):
    g0: LineSegment StartX=-11.5069 StartY=93.2653 StartZ=0 EndX=11.5069 EndY=93.2653 EndZ=0
    g1: LineSegment StartX=6.25 StartY=89.2653 StartZ=0 EndX=-6.25 EndY=89.2653 EndZ=0
    g2: LineSegment StartX=-11.5069 StartY=93.2653 StartZ=0 EndX=-20.6582 EndY=72.2653 EndZ=0
    g3: LineSegment StartX=-20.6582 StartY=72.2653 StartZ=0 EndX=-20.6582 EndY=68.2653 EndZ=0
    g4: LineSegment StartX=-20.6582 StartY=68.2653 StartZ=0 EndX=-6.25 EndY=68.2653 EndZ=0
    g5: LineSegment StartX=-9.25 StartY=72.2653 StartZ=0 EndX=-16.6582 EndY=72.2653 EndZ=0
    g6: LineSegment StartX=-16.6582 StartY=72.2653 StartZ=0 EndX=-9.25 EndY=89.2653 EndZ=0
    g7: LineSegment StartX=-6.25 StartY=89.2653 StartZ=0 EndX=-6.25 EndY=68.2653 EndZ=0
    g8: LineSegment StartX=-9.25 StartY=72.2653 StartZ=0 EndX=-9.25 EndY=89.2653 EndZ=0
    g9: LineSegment StartX=9.25 StartY=89.2653 StartZ=0 EndX=9.25 EndY=72.2653 EndZ=0
    g10: LineSegment StartX=9.25 StartY=72.2653 StartZ=0 EndX=16.6582 EndY=72.2653 EndZ=0
    g11: LineSegment StartX=6.25 StartY=89.2653 StartZ=0 EndX=6.25 EndY=68.2653 EndZ=0
    g12: LineSegment StartX=6.25 StartY=68.2653 StartZ=0 EndX=20.6582 EndY=68.2653 EndZ=0
    g13: LineSegment StartX=20.6582 StartY=68.2653 StartZ=0 EndX=20.6582 EndY=72.2653 EndZ=0
    g14: LineSegment StartX=20.6582 StartY=72.2653 StartZ=0 EndX=11.5069 EndY=93.2653 EndZ=0
    g15: LineSegment StartX=16.6582 StartY=72.2653 StartZ=0 EndX=9.25 EndY=89.2653 EndZ=0
  constraints (40):
    c: Symmetric(g0,g0,g-2)
    c: Coincident(g2,g0)
    c: Coincident(g3,g2)
    c: Vertical(g3)
    c: Coincident(g4,g3)
    c: Horizontal(g4)
    c: Horizontal(g5)
    c: Coincident(g6,g5)
    c: Vertical(g7)
    c: Vertical(g8)
    c: Coincident(g1,g7)
    c: Coincident(g4,g7)
    c: Parallel(g2,g6)
    c: Coincident(g6,g8)
    c: Coincident(g5,g8)
    c: PointOnObject(g6,g1)
    c: PointOnObject(g2,g5)
    c: Vertical(g9)
    c: Coincident(g10,g9)
    c: Coincident(g12,g11)
    c: Horizontal(g12)
    c: Coincident(g13,g12)
    c: Vertical(g13)
    c: Coincident(g14,g13)
    c: Coincident(g14,g0)
    c: Coincident(g15,g10)
    c: Coincident(g1,g11)
    c: Symmetric(g4,g11,g-2)
    c: Symmetric(g9,g5,g-2)
    c: Coincident(g9,g15)
    c: Symmetric(g1,g1,g-2)
    c: PointOnObject(g9,g1)
    c: Symmetric(g10,g5,g-2)
    c: Symmetric(g2,g13,g-2)
    c: DistanceY(g3,g5) = 4
    c: DistanceX(g5,g4) = 3
    c: DistanceX(g2,g5) = 4
    c: DistanceY(g6,g0) = 4
    c: DistanceY(g7,g7) = 21
    c: DistanceX(g1,g1) = 12.5
FEATURE [PartDesign::Pad] Pad024  label="pad_servo_clip_base"
  Direction = (0,0,1)
  Length = 15
  Length2 = 10
  Midplane = true
  Profile = -> Sketch061
  Refine = true
  Type = 0
FEATURE [Sketcher::SketchObject] Sketch062  label="sk_servo_clip_top_cutout"
  AttachmentOffset = pos=(0,0,-94) rot=(0,0,1;0rad)
  FullyConstrained = false
  MapMode = 5
  Placement = pos=(0,94,2.09e-14) rot=(1,0,0;1.5708rad)
  Support = -> [XZ_Plane012]
  expr: Constraints[10] = <<sk_valve_top_connect_holes>>.Constraints.rear_distance + <<pad_servo_clip_base>>.Length / 2 - 4mm
  expr: Constraints[8] = <<sk_valve_top_connect_holes>>.Constraints.rear_distance
  sketch-geometry (5):
    g0: LineSegment StartX=22.6609 StartY=23.05 StartZ=0 EndX=6.26943 EndY=23.05 EndZ=0
    g1: LineSegment StartX=6.26943 StartY=23.05 StartZ=0 EndX=6.26943 EndY=16.05 EndZ=0
    g2: LineSegment StartX=6.26943 StartY=16.05 StartZ=0 EndX=22.6609 EndY=16.05 EndZ=0
    g3: LineSegment StartX=22.6609 StartY=16.05 StartZ=0 EndX=22.6609 EndY=23.05 EndZ=0
    g4: GeomPoint X=6.26943 Y=19.55 Z=0
  constraints (12):
    c: Coincident(g0,g1)
    c: Coincident(g1,g2)
    c: Coincident(g2,g3)
    c: Coincident(g3,g0)
    c: Horizontal(g0)
    c: Horizontal(g2)
    c: Vertical(g1)
    c: Vertical(g3)
    c: DistanceY(g-1,g4) = 19.55
    c: Symmetric(g0,g1,g4)
    c: DistanceY(g-1,g0) = 23.05
    c: DistanceY(g3,g3) = 7
FEATURE [PartDesign::Pocket] Pocket003023  label="pocket_servo_clip_top_cutout"
  BaseFeature = -> Pad024
  Direction = (0,1,2e-16)
  Length = 22
  Length2 = 5
  Profile = -> Sketch062
  Refine = true
  Reversed = true
  Type = 0
FEATURE [PartDesign::Mirrored] Mirrored003  label="mirror_servo_clip_top_cutout"
  BaseFeature = -> Pocket003023
  MirrorPlane = -> Sketch062 [V_Axis]
  Originals = -> [Pocket003023]
  Refine = true
FEATURE [PartDesign::Pocket] Pocket003024  label="pocket_servo_clip_mount_holes"
  BaseFeature = -> Mirrored003
  Direction = (0,1,2e-16)
  Length = 5
  Length2 = 5
  Profile = -> Sketch060
  Refine = true
  Reversed = true
  Type = 1
FEATURE [Sketcher::SketchObject] Sketch063  label="sk_servo_clip_cable_channel"
  AttachmentOffset = pos=(0,0,-89) rot=(0,0,1;0rad)
  FullyConstrained = false
  MapMode = 5
  Placement = pos=(0,89,1.98e-14) rot=(1,0,0;1.5708rad)
  Support = -> [XZ_Plane012]
  sketch-geometry (4):
    g0: LineSegment StartX=-2 StartY=26.6105 StartZ=0 EndX=2 EndY=26.6105 EndZ=0
    g1: LineSegment StartX=2 StartY=26.6105 StartZ=0 EndX=2 EndY=13.7541 EndZ=0
    g2: LineSegment StartX=2 StartY=13.7541 StartZ=0 EndX=-2 EndY=13.7541 EndZ=0
    g3: LineSegment StartX=-2 StartY=13.7541 StartZ=0 EndX=-2 EndY=26.6105 EndZ=0
  constraints (9):
    c: Coincident(g0,g1)
    c: Coincident(g1,g2)
    c: Coincident(g2,g3)
    c: Coincident(g3,g0)
    c: Horizontal(g2)
    c: Vertical(g1)
    c: Vertical(g3)
    c: Symmetric(g0,g0,g-2)
    c: DistanceX(g2,g2) = 4  'servo_cable_channel_width'
FEATURE [PartDesign::Pocket] Pocket003025  label="pocket_servo_clip_cable_channel"
  BaseFeature = -> Pocket003024
  Direction = (0,1,2e-16)
  Length = 2
  Length2 = 5
  Profile = -> Sketch063
  Refine = true
  Type = 0
FEATURE [PartDesign::Body] Body012  label="servo_clip"
  Group = -> [Sketch060,Sketch061,Pad024,Sketch062,Pocket003023,Mirrored003,Pocket003024,Sketch063,Pocket003025]
  Origin = -> Origin012
  Placement = pos=(0,2.5,0) rot=(0,0,1;0rad)
  Tip = -> Pocket003025
FEATURE [Sketcher::SketchObject] Sketch064  label="sk_valve_front_taper007"
  FullyConstrained = true
  MapMode = 5
  Support = -> [XY_Plane013]
  expr: Constraints[2] = <<sk_fanduct_base>>.Constraints.duct_hole_diameter - 1mm
  expr: Constraints[3] = <<sk_fanduct_base>>.Constraints.duct_hole_diameter - 3mm
  sketch-geometry (2):
    g0: Circle CenterX=0 CenterY=0 CenterZ=0 NormalX=0 NormalY=0 NormalZ=1 AngleXU=0 Radius=37.65
    g1: Circle CenterX=0 CenterY=0 CenterZ=0 NormalX=0 NormalY=0 NormalZ=1 AngleXU=0 Radius=36.65
  constraints (4):
    c: Coincident(g0,g-1)
    c: Coincident(g1,g0)
    c: Diameter(g0) = 75.3
    c: Diameter(g1) = 73.3
FEATURE [PartDesign::Pad] Pad025
  Direction = (0,0,1)
  Length = 10
  Length2 = 10
  Profile = -> Sketch064
  Refine = true
  Type = 0
FEATURE [Sketcher::SketchObject] Sketch065  label="sk_valve_front_taper008"
  AttachmentOffset = pos=(0,0,15) rot=(0,0,1;0rad)
  FullyConstrained = true
  MapMode = 5
  Placement = pos=(0,0,15) rot=(0,0,1;0rad)
  Support = -> [XY_Plane013]
  expr: .AttachmentOffset.Base.z = <<Pad025>>.Length + 5mm
  expr: Constraints[2] = <<Spreadsheet>>.front_led_ring_outer_diameter + 3mm
  expr: Constraints[3] = <<sk_fanduct_base>>.Constraints.duct_hole_diameter - 3mm
  sketch-geometry (2):
    g0: Circle CenterX=0 CenterY=0 CenterZ=0 NormalX=0 NormalY=0 NormalZ=1 AngleXU=0 Radius=49.5
    g1: Circle CenterX=0 CenterY=0 CenterZ=0 NormalX=0 NormalY=0 NormalZ=1 AngleXU=0 Radius=36.65
  constraints (4):
    c: Coincident(g0,g-1)
    c: Coincident(g1,g0)
    c: Diameter(g0) = 99
    c: Diameter(g1) = 73.3
FEATURE [Sketcher::SketchObject] Sketch066  label="sk_valve_front_taper009"
  AttachmentOffset = pos=(0,0,10) rot=(0,0,1;0rad)
  FullyConstrained = true
  MapMode = 5
  Placement = pos=(0,0,10) rot=(0,0,1;0rad)
  Support = -> [XY_Plane013]
  expr: .AttachmentOffset.Base.z = <<Pad025>>.Length
  expr: Constraints[2] = <<sk_fanduct_base>>.Constraints.duct_hole_diameter - 1mm
  expr: Constraints[3] = <<sk_fanduct_base>>.Constraints.duct_hole_diameter - 3mm
  sketch-geometry (2):
    g0: Circle CenterX=0 CenterY=0 CenterZ=0 NormalX=0 NormalY=0 NormalZ=1 AngleXU=0 Radius=37.65
    g1: Circle CenterX=0 CenterY=0 CenterZ=0 NormalX=0 NormalY=0 NormalZ=1 AngleXU=0 Radius=36.65
  constraints (4):
    c: Coincident(g0,g-1)
    c: Coincident(g1,g0)
    c: Diameter(g0) = 75.3
    c: Diameter(g1) = 73.3
FEATURE [PartDesign::AdditiveLoft] AdditiveLoft003
  BaseFeature = -> Pad025
  Closed = false
  Profile = -> Sketch065
  Refine = true
  Ruled = false
  Sections = -> [Sketch066]
FEATURE [Sketcher::SketchObject] Sketch067  label="sk_valve_front_taper010"
  AttachmentOffset = pos=(0,0,25) rot=(0,0,1;0rad)
  FullyConstrained = true
  MapMode = 5
  Placement = pos=(0,0,25) rot=(0,0,1;0rad)
  Support = -> [XY_Plane013]
  expr: .AttachmentOffset.Base.z = <<Pad025>>.Length + 15mm
  expr: Constraints[2] = <<Spreadsheet>>.front_led_ring_outer_diameter + 3mm
  expr: Constraints[3] = <<sk_fanduct_base>>.Constraints.duct_hole_diameter - 3mm
  sketch-geometry (2):
    g0: Circle CenterX=0 CenterY=0 CenterZ=0 NormalX=0 NormalY=0 NormalZ=1 AngleXU=0 Radius=49.5
    g1: Circle CenterX=0 CenterY=0 CenterZ=0 NormalX=0 NormalY=0 NormalZ=1 AngleXU=0 Radius=36.65
  constraints (4):
    c: Coincident(g0,g-1)
    c: Coincident(g1,g0)
    c: Diameter(g0) = 99
    c: Diameter(g1) = 73.3
FEATURE [PartDesign::Pad] Pad026
  BaseFeature = -> AdditiveLoft003
  Direction = (0,0,1)
  Length = 10
  Length2 = 10
  Profile = -> Sketch067
  Refine = true
  Reversed = true
  Type = 0
FEATURE [Sketcher::SketchObject] Sketch068  label="sk_valve_front_taper011"
  AttachmentOffset = pos=(0,0,25) rot=(0,0,1;0rad)
  FullyConstrained = true
  MapMode = 5
  Placement = pos=(0,0,25) rot=(0,0,1;0rad)
  Support = -> [XY_Plane013]
  expr: .AttachmentOffset.Base.z = <<Pad025>>.Length + 15mm
  expr: Constraints[2] = <<Spreadsheet>>.front_led_ring_outer_diameter + 1mm
  expr: Constraints[3] = <<Spreadsheet>>.front_led_ring_inner_diameter - 1mm
  sketch-geometry (2):
    g0: Circle CenterX=0 CenterY=0 CenterZ=0 NormalX=0 NormalY=0 NormalZ=1 AngleXU=0 Radius=48.5
    g1: Circle CenterX=0 CenterY=0 CenterZ=0 NormalX=0 NormalY=0 NormalZ=1 AngleXU=0 Radius=38.5
  constraints (4):
    c: Coincident(g0,g-1)
    c: Coincident(g1,g0)
    c: Diameter(g0) = 97
    c: Diameter(g1) = 77
FEATURE [PartDesign::Pocket] Pocket003026
  BaseFeature = -> Pad026
  Direction = (0,0,-1)
  Length = 5
  Length2 = 5
  Profile = -> Sketch068
  Refine = true
  Type = 0
FEATURE [PartDesign::Body] Body013
  Group = -> [Sketch064,Pad025,Sketch065,Sketch066,AdditiveLoft003,Sketch067,Pad026,Sketch068,Pocket003026]
  Origin = -> Origin013
  Placement = pos=(0,0,98) rot=(0,0,1;0rad)
  Tip = -> Pocket003026
FEATURE [Mesh::Feature] Mesh  label="pocket_servo_clip_cable_channel (Meshed)"
FEATURE [Sketcher::SketchObject] Sketch069  label="sk_valve_main_axis001"
  AttachmentOffset = pos=(0,24,-50) rot=(0,0,1;0rad)
  FullyConstrained = true
  MapMode = 5
  Placement = pos=(0,50,24) rot=(1,0,0;1.5708rad)
  Support = -> [XZ_Plane006]
  expr: .AttachmentOffset.Base.z = Sketch009.Constraints.top_border * -1
  sketch-geometry (1):
    g0: Circle CenterX=0 CenterY=0 CenterZ=0 NormalX=0 NormalY=0 NormalZ=1 AngleXU=0 Radius=2.45
  constraints (2):
    c: Coincident(g0,g-1)
    c: Diameter(g0) = 4.9  'main_axis_diameter'
FEATURE [Sketcher::SketchObject] Sketch041  label="sk_servo_hold_top_cutout"
  AttachmentOffset = pos=(0,0,-71) rot=(0,0,1;0rad)
  ExternalGeometry = -> [Sketch069]
  FullyConstrained = true
  MapMode = 5
  Placement = pos=(0,71,1.58e-14) rot=(1,0,0;1.5708rad)
  Support = -> [XZ_Plane006]
  sketch-geometry (4):
    g0: LineSegment StartX=6.5 StartY=32.22 StartZ=0 EndX=-6.5 EndY=32.22 EndZ=0
    g1: LineSegment StartX=-6.5 StartY=32.22 StartZ=0 EndX=-6.5 EndY=9 EndZ=0
    g2: LineSegment StartX=-6.5 StartY=9 StartZ=0 EndX=6.5 EndY=9 EndZ=0
    g3: LineSegment StartX=6.5 StartY=9 StartZ=0 EndX=6.5 EndY=32.22 EndZ=0
  constraints (11):
    c: Coincident(g0,g1)
    c: Coincident(g1,g2)
    c: Coincident(g2,g3)
    c: Coincident(g3,g0)
    c: Horizontal(g2)
    c: Vertical(g1)
    c: Vertical(g3)
    c: DistanceX(g0,g0) = 13
    c: DistanceY(g1,g1) = 23.22
    c: Symmetric(g0,g0,g-2)
    c: DistanceY(g-3,g0) = 8.22
FEATURE [PartDesign::Pocket] Pocket003014  label="pocket_servo_hold_top_cutout"
  BaseFeature = -> Pad017
  Direction = (0,1,2e-16)
  Length = 0
  Length2 = 5
  Profile = -> Sketch041
  Refine = true
  Reversed = true
  Type = 1
FEATURE [PartDesign::Pocket] Pocket003015  label="pocket_servo_hold_front_cutout"
  BaseFeature = -> Pocket003014
  Direction = (0,0,-1)
  Length = 5
  Length2 = 5
  Profile = -> Sketch042
  Refine = true
  Type = 1
FEATURE [PartDesign::Pocket] Pocket003016  label="pocket_servo_hold_side_cutout"
  BaseFeature = -> Pocket003015
  Direction = (-1,2e-16,-3e-16)
  Length = 5
  Length2 = 5
  Profile = -> Sketch043
  Refine = true
  Type = 1
FEATURE [PartDesign::Pocket] Pocket003019  label="pocket_servo_hold_top_holes"
  BaseFeature = -> Pocket003016
  Direction = (0,1,2e-16)
  Length = 5
  Length2 = 5
  Profile = -> Sketch050
  Refine = true
  Reversed = true
  Type = 1
FEATURE [PartDesign::Body] Body006  label="servo_hold"
  Group = -> [Sketch040,Pad017,Sketch041,Pocket003014,Sketch042,Pocket003015,Sketch043,Pocket003016,Sketch050,Pocket003019,Sketch069]
  Origin = -> Origin006
  Tip = -> Pocket003019
FEATURE [App::DocumentObjectGroup] Group002  label="Servo"
  Group = -> [Body006,Body012,Fusion007001]
FEATURE [Sketcher::SketchObject] Sketch070  label="sk_fan_duct_connector_cut"
  AttachmentOffset = pos=(0,0,50) rot=(0,0,1;0rad)
  FullyConstrained = true
  MapMode = 5
  Placement = pos=(0,0,50) rot=(0,0,1;0rad)
  Support = -> [XY_Plane014]
  expr: .AttachmentOffset.Base.z = <<pad_fan_duct_connector>>.Length
  expr: Constraints[2] = <<Spreadsheet>>.duct_hole_diameter - 0.5mm
  expr: Constraints[3] = <<Spreadsheet>>.pipe_outer_diameter + 0.5mm
  sketch-geometry (2):
    g0: Circle CenterX=0 CenterY=0 CenterZ=0 NormalX=0 NormalY=0 NormalZ=1 AngleXU=0 Radius=37.9
    g1: Circle CenterX=0 CenterY=0 CenterZ=0 NormalX=0 NormalY=0 NormalZ=1 AngleXU=0 Radius=40.4
  constraints (4):
    c: Coincident(g0,g-1)
    c: Coincident(g1,g0)
    c: Diameter(g0) = 75.8
    c: Diameter(g1) = 80.8
FEATURE [Sketcher::SketchObject] Sketch071  label="sk_fan_duct_connector"
  FullyConstrained = true
  MapMode = 5
  Support = -> [XY_Plane014]
  expr: Constraints[2] = <<Spreadsheet>>.duct_hole_diameter - <<Spreadsheet>>.pipe_width
  expr: Constraints[3] = <<Spreadsheet>>.pipe_outer_diameter + <<Spreadsheet>>.pipe_width
  sketch-geometry (2):
    g0: Circle CenterX=0 CenterY=0 CenterZ=0 NormalX=0 NormalY=0 NormalZ=1 AngleXU=0 Radius=36.15
    g1: Circle CenterX=0 CenterY=0 CenterZ=0 NormalX=0 NormalY=0 NormalZ=1 AngleXU=0 Radius=42.15
  constraints (4):
    c: Coincident(g0,g-1)
    c: Coincident(g1,g0)
    c: Diameter(g0) = 72.3
    c: Diameter(g1) = 84.3
FEATURE [PartDesign::Pad] Pad027  label="pad_fan_duct_connector"
  Direction = (0,0,1)
  Length = 50
  Length2 = 10
  Profile = -> Sketch071
  ReferenceAxis = -> Sketch071 [N_Axis]
  Refine = true
  Type = 0
FEATURE [PartDesign::Pocket] Pocket003027  label="pocket_fan_duct_connector_cut"
  BaseFeature = -> Pad027
  Direction = (0,0,-1)
  Length = 20
  Length2 = 5
  Profile = -> Sketch070
  ReferenceAxis = -> Sketch070 [N_Axis]
  Refine = true
  Type = 0
FEATURE [Sketcher::SketchObject] Sketch073  label="sk_fan_duct_start"
  FullyConstrained = true
  MapMode = 5
  Support = -> [XY_Plane014]
  expr: Constraints[2] = <<Spreadsheet>>.duct_hole_diameter - <<Spreadsheet>>.pipe_width
  expr: Constraints[3] = <<Spreadsheet>>.pipe_outer_diameter + <<Spreadsheet>>.pipe_width
  sketch-geometry (2):
    g0: Circle CenterX=0 CenterY=0 CenterZ=0 NormalX=0 NormalY=0 NormalZ=1 AngleXU=0 Radius=36.15
    g1: Circle CenterX=0 CenterY=0 CenterZ=0 NormalX=0 NormalY=0 NormalZ=1 AngleXU=0 Radius=42.15
  constraints (4):
    c: Coincident(g0,g-1)
    c: Coincident(g1,g0)
    c: Diameter(g0) = 72.3
    c: Diameter(g1) = 84.3
FEATURE [Sketcher::SketchObject] Sketch074  label="sk_fan_duct_end"
  AttachmentOffset = pos=(0,0,-45) rot=(0,0,1;0rad)
  FullyConstrained = true
  MapMode = 5
  Placement = pos=(0,0,-45) rot=(0,0,1;0rad)
  Support = -> [XY_Plane014]
  expr: .AttachmentOffset.Base.z = -<<Spreadsheet>>.fan_duct_depth
  expr: Constraints[10] = <<Spreadsheet>>.fan_duct_width
  expr: Constraints[2] = <<Spreadsheet>>.duct_hole_diameter - <<Spreadsheet>>.pipe_width
  sketch-geometry (7):
    g0: Circle CenterX=0 CenterY=0 CenterZ=0 NormalX=0 NormalY=0 NormalZ=1 AngleXU=0 Radius=36.15
    g1: ArcOfCircle CenterX=0 CenterY=0 CenterZ=0 NormalX=0 NormalY=0 NormalZ=1 AngleXU=0 Radius=70.7107 StartAngle=5.49779 EndAngle=10.2102
    g2: LineSegment StartX=-50 StartY=50 StartZ=0 EndX=50 EndY=50 EndZ=0
    g3: LineSegment StartX=50 StartY=50 StartZ=0 EndX=50 EndY=-50 EndZ=0
    g4: LineSegment StartX=50 StartY=-50 StartZ=0 EndX=-50 EndY=-50 EndZ=0
    g5: LineSegment StartX=-50 StartY=-50 StartZ=0 EndX=-50 EndY=50 EndZ=0
    g6: LineSegment StartX=-50 StartY=-50 StartZ=0 EndX=50 EndY=-50 EndZ=0
  constraints (17):
    c: Coincident(g0,g-1)
    c: Coincident(g1,g0)
    c: Diameter(g0) = 72.3
    c: Coincident(g2,g3)
    c: Coincident(g3,g4)
    c: Coincident(g4,g5)
    c: Coincident(g5,g2)
    c: Horizontal(g2)
    c: Horizontal(g4)
    c: Vertical(g3)
    c: DistanceX(g2,g2) = 100
    c: Equal(g2,g3)
    c: Symmetric(g2,g3,g0)
    c: Coincident(g6,g4)
    c: Coincident(g6,g3)
    c: Coincident(g1,g4)
    c: Coincident(g1,g3)
FEATURE [Sketcher::SketchObject] Sketch075  label="sk_fan_cutout"
  AttachmentOffset = pos=(0,0,-55) rot=(0,0,1;0rad)
  FullyConstrained = true
  MapMode = 5
  Placement = pos=(0,0,-55) rot=(0,0,1;0rad)
  Support = -> [XY_Plane014]
  expr: .AttachmentOffset.Base.z = -<<Spreadsheet>>.fan_duct_depth + <<Spreadsheet>>.fan_mount_overhang - <<Spreadsheet>>.fan_mount_depth / 2
  expr: .Constraints.fan_width = <<Spreadsheet>>.fan_mount_width
  expr: Constraints[5] = 82mm
  sketch-geometry (5):
    g0: LineSegment StartX=-41 StartY=-59 StartZ=0 EndX=-41 EndY=41 EndZ=0
    g1: LineSegment StartX=-41 StartY=41 StartZ=0 EndX=41 EndY=41 EndZ=0
    g2: LineSegment StartX=41 StartY=41 StartZ=0 EndX=41 EndY=-59 EndZ=0
    g3: LineSegment StartX=41 StartY=-59 StartZ=0 EndX=-41 EndY=-59 EndZ=0
    g4: GeomPoint X=0 Y=0 Z=0
  constraints (12):
    c: Horizontal(g3)
    c: Vertical(g0)
    c: Vertical(g2)
    c: Coincident(g4,g-1)
    c: DistanceY(g2,g2) = 100  'fan_width'
    c: DistanceX(g3,g3) = 82
    c: Symmetric(g0,g1,g-2)
    c: DistanceY(g4,g1) = 41
    c: Coincident(g0,g1)
    c: Coincident(g0,g3)
    c: Coincident(g2,g3)
    c: Coincident(g1,g2)
FEATURE [PartDesign::AdditiveLoft] AdditiveLoft004  label="loft_fan_duct"
  BaseFeature = -> Pocket003027
  Closed = true
  Profile = -> Sketch073
  Refine = true
  Ruled = false
  Sections = -> [Sketch074]
FEATURE [Sketcher::SketchObject] Sketch083  label="sk_fan_hold"
  AttachmentOffset = pos=(0,0,-30) rot=(0,0,1;0rad)
  FullyConstrained = true
  MapMode = 5
  Placement = pos=(0,0,-30) rot=(0,0,1;0rad)
  Support = -> [XY_Plane014]
  expr: .AttachmentOffset.Base.z = -<<Spreadsheet>>.fan_duct_depth + <<Spreadsheet>>.fan_mount_overhang
  expr: Constraints[10] = <<Spreadsheet>>.fan_mount_width
  expr: Constraints[2] = <<Spreadsheet>>.duct_hole_diameter - <<Spreadsheet>>.pipe_width
  sketch-geometry (7):
    g0: Circle CenterX=0 CenterY=0 CenterZ=0 NormalX=0 NormalY=0 NormalZ=1 AngleXU=0 Radius=36.15
    g1: ArcOfCircle CenterX=0 CenterY=0 CenterZ=0 NormalX=0 NormalY=0 NormalZ=1 AngleXU=0 Radius=70.7107 StartAngle=5.49779 EndAngle=10.2102
    g2: LineSegment StartX=-50 StartY=50 StartZ=0 EndX=50 EndY=50 EndZ=0
    g3: LineSegment StartX=50 StartY=50 StartZ=0 EndX=50 EndY=-50 EndZ=0
    g4: LineSegment StartX=50 StartY=-50 StartZ=0 EndX=-50 EndY=-50 EndZ=0
    g5: LineSegment StartX=-50 StartY=-50 StartZ=0 EndX=-50 EndY=50 EndZ=0
    g6: LineSegment StartX=-50 StartY=-50 StartZ=0 EndX=50 EndY=-50 EndZ=0
  constraints (18):
    c: Coincident(g0,g-1)
    c: Coincident(g1,g0)
    c: Diameter(g0) = 72.3
    c: Coincident(g2,g3)
    c: Coincident(g3,g4)
    c: Coincident(g4,g5)
    c: Coincident(g5,g2)
    c: Horizontal(g2)
    c: Horizontal(g4)
    c: Vertical(g3)
    c: DistanceX(g2,g2) = 100
    c: Equal(g2,g3)
    c: Symmetric(g2,g3,g0)
    c: Coincident(g6,g4)
    c: Coincident(g6,g3)
    c: Coincident(g1,g4)
    c: Coincident(g1,g3)
    c: Radius(g1) = 70.7107
FEATURE [PartDesign::Pad] Pad028  label="pad_fan_hold"
  BaseFeature = -> AdditiveLoft004
  Direction = (0,0,1)
  Length = 50
  Length2 = 10
  Profile = -> Sketch083
  ReferenceAxis = -> Sketch083 [N_Axis]
  Refine = true
  Reversed = true
  Type = 0
  expr: Length = <<Spreadsheet>>.fan_mount_depth
FEATURE [Sketcher::SketchObject] Sketch084  label="sk_fan_mounting_holes"
  AttachmentOffset = pos=(0,0,-80) rot=(0,0,1;0rad)
  FullyConstrained = true
  MapMode = 5
  Placement = pos=(0,0,-80) rot=(0,0,1;0rad)
  Support = -> [XY_Plane014]
  expr: .AttachmentOffset.Base.z = -<<Spreadsheet>>.fan_duct_depth + <<Spreadsheet>>.fan_mount_overhang - <<Spreadsheet>>.fan_mount_depth
  expr: .Constraints.mounting_hole_diameter = <<Spreadsheet>>.fan_mounting_hole_diameter
  expr: .Constraints.mounting_holes_distance = <<Spreadsheet>>.fan_mounting_hole_distance
  expr: Constraints[6] = .Constraints.mounting_holes_distance
  sketch-geometry (5):
    g0: GeomPoint X=0 Y=0 Z=0
    g1: Circle CenterX=-35.75 CenterY=35.75 CenterZ=0 NormalX=0 NormalY=0 NormalZ=1 AngleXU=0 Radius=2.15
    g2: Circle CenterX=35.75 CenterY=35.75 CenterZ=0 NormalX=0 NormalY=0 NormalZ=1 AngleXU=0 Radius=2.15
    g3: Circle CenterX=35.75 CenterY=-35.75 CenterZ=0 NormalX=0 NormalY=0 NormalZ=1 AngleXU=0 Radius=2.15
    g4: Circle CenterX=-35.75 CenterY=-35.75 CenterZ=0 NormalX=0 NormalY=0 NormalZ=1 AngleXU=0 Radius=2.15
  constraints (10):
    c: Coincident(g0,g-1)
    c: Equal(g4,g3)
    c: Equal(g3,g2)
    c: Equal(g2,g1)
    c: Symmetric(g3,g4,g-2)
    c: DistanceX(g1,g2) = 71.5  'mounting_holes_distance'
    c: DistanceY(g3,g2) = 71.5
    c: Diameter(g1) = 4.3  'mounting_hole_diameter'
    c: Symmetric(g4,g2,g0)
    c: Symmetric(g1,g3,g0)
FEATURE [PartDesign::Pocket] Pocket003028  label="pocket_sk_fan_mounting_holes"
  BaseFeature = -> Pad028
  Direction = (0,0,-1)
  Length = 5
  Length2 = 5
  Profile = -> Sketch084
  ReferenceAxis = -> Sketch084 [N_Axis]
  Refine = true
  Reversed = true
  Type = 1
FEATURE [PartDesign::Pocket] Pocket003029  label="pocket_fan_cutout"
  BaseFeature = -> Pocket003028
  Direction = (0,0,-1)
  Length = 35
  Length2 = 5
  Midplane = true
  Profile = -> Sketch075
  ReferenceAxis = -> Sketch075 [N_Axis]
  Refine = true
  Type = 0
  expr: Length = <<Spreadsheet>>.fan_depth
FEATURE [Sketcher::SketchObject] Sketch085  label="sk_fan_mounting_nuts"
  AttachmentOffset = pos=(0,0,-80) rot=(0,0,1;0rad)
  FullyConstrained = true
  MapMode = 5
  Placement = pos=(0,0,-80) rot=(0,0,1;0rad)
  Support = -> [XY_Plane014]
  expr: .AttachmentOffset.Base.z = -<<Spreadsheet>>.fan_duct_depth + <<Spreadsheet>>.fan_mount_overhang - <<Spreadsheet>>.fan_mount_depth
  expr: Constraints[69] = <<Spreadsheet>>.fan_mounting_hole_distance
  expr: Constraints[80] = <<Spreadsheet>>.m4_nut_distance
  expr: Constraints[81] = <<Spreadsheet>>.fan_mounting_hole_distance
  sketch-geometry (29):
    g0: GeomPoint X=0 Y=0 Z=0
    g1: LineSegment StartX=-33.825 StartY=32.4158 StartZ=0 EndX=-31.9 EndY=35.75 EndZ=0
    g2: LineSegment StartX=-31.9 StartY=35.75 StartZ=0 EndX=-33.825 EndY=39.0842 EndZ=0
    g3: LineSegment StartX=-33.825 StartY=39.0842 StartZ=0 EndX=-37.675 EndY=39.0842 EndZ=0
    g4: LineSegment StartX=-37.675 StartY=39.0842 StartZ=0 EndX=-39.6 EndY=35.75 EndZ=0
    g5: LineSegment StartX=-39.6 StartY=35.75 StartZ=0 EndX=-37.675 EndY=32.4158 EndZ=0
    g6: LineSegment StartX=-37.675 StartY=32.4158 StartZ=0 EndX=-33.825 EndY=32.4158 EndZ=0
    g7: Circle CenterX=-35.75 CenterY=35.75 CenterZ=0 NormalX=0 NormalY=0 NormalZ=1 AngleXU=0 Radius=3.85
    g8: LineSegment StartX=37.675 StartY=32.4158 StartZ=0 EndX=39.6 EndY=35.75 EndZ=0
    g9: LineSegment StartX=39.6 StartY=35.75 StartZ=0 EndX=37.675 EndY=39.0842 EndZ=0
    g10: LineSegment StartX=37.675 StartY=39.0842 StartZ=0 EndX=33.825 EndY=39.0842 EndZ=0
    g11: LineSegment StartX=33.825 StartY=39.0842 StartZ=0 EndX=31.9 EndY=35.75 EndZ=0
    g12: LineSegment StartX=31.9 StartY=35.75 StartZ=0 EndX=33.825 EndY=32.4158 EndZ=0
    g13: LineSegment StartX=33.825 StartY=32.4158 StartZ=0 EndX=37.675 EndY=32.4158 EndZ=0
    g14: Circle CenterX=35.75 CenterY=35.75 CenterZ=0 NormalX=0 NormalY=0 NormalZ=1 AngleXU=0 Radius=3.85
    g15: LineSegment StartX=37.675 StartY=-39.0842 StartZ=0 EndX=39.6 EndY=-35.75 EndZ=0
    g16: LineSegment StartX=39.6 StartY=-35.75 StartZ=0 EndX=37.675 EndY=-32.4158 EndZ=0
    g17: LineSegment StartX=37.675 StartY=-32.4158 StartZ=0 EndX=33.825 EndY=-32.4158 EndZ=0
    g18: LineSegment StartX=33.825 StartY=-32.4158 StartZ=0 EndX=31.9 EndY=-35.75 EndZ=0
    g19: LineSegment StartX=31.9 StartY=-35.75 StartZ=0 EndX=33.825 EndY=-39.0842 EndZ=0
    g20: LineSegment StartX=33.825 StartY=-39.0842 StartZ=0 EndX=37.675 EndY=-39.0842 EndZ=0
    g21: Circle CenterX=35.75 CenterY=-35.75 CenterZ=0 NormalX=0 NormalY=0 NormalZ=1 AngleXU=0 Radius=3.85
    g22: LineSegment StartX=-33.825 StartY=-39.0842 StartZ=0 EndX=-31.9 EndY=-35.75 EndZ=0
    g23: LineSegment StartX=-31.9 StartY=-35.75 StartZ=0 EndX=-33.825 EndY=-32.4158 EndZ=0
    g24: LineSegment StartX=-33.825 StartY=-32.4158 StartZ=0 EndX=-37.675 EndY=-32.4158 EndZ=0
    g25: LineSegment StartX=-37.675 StartY=-32.4158 StartZ=0 EndX=-39.6 EndY=-35.75 EndZ=0
    g26: LineSegment StartX=-39.6 StartY=-35.75 StartZ=0 EndX=-37.675 EndY=-39.0842 EndZ=0
    g27: LineSegment StartX=-37.675 StartY=-39.0842 StartZ=0 EndX=-33.825 EndY=-39.0842 EndZ=0
    g28: Circle CenterX=-35.75 CenterY=-35.75 CenterZ=0 NormalX=0 NormalY=0 NormalZ=1 AngleXU=0 Radius=3.85
  constraints (66):
    c: Coincident(g0,g-1)
    c: Coincident(g1,g2)
    c: Coincident(g2,g3)
    c: Coincident(g3,g4)
    c: Coincident(g4,g5)
    c: Coincident(g5,g6)
    c: Coincident(g6,g1)
    c: Equal(g1, g2-g6) x5
    c: PointOnObject(g1,g7)
    c: PointOnObject(g2,g7)
    c: PointOnObject(g3,g7)
    c: PointOnObject(g4,g7)
    c: PointOnObject(g5,g7)
    c: PointOnObject(g6,g7)
    c: Coincident(g8,g9)
    c: Coincident(g9,g10)
    c: Coincident(g10,g11)
    c: Coincident(g11,g12)
    c: Coincident(g12,g13)
    c: Coincident(g13,g8)
    c: Equal(g8, g9-g13) x5
    c: PointOnObject(g8,g14)
    c: PointOnObject(g9,g14)
    c: PointOnObject(g10,g14)
    c: PointOnObject(g11,g14)
    c: PointOnObject(g12,g14)
    c: PointOnObject(g13,g14)
    c: Coincident(g15,g16)
    c: Coincident(g16,g17)
    c: Coincident(g17,g18)
    c: Coincident(g18,g19)
    c: Coincident(g19,g20)
    c: Coincident(g20,g15)
    c: Equal(g15, g16-g20) x5
    c: PointOnObject(g15,g21)
    c: PointOnObject(g16,g21)
    c: PointOnObject(g17,g21)
    c: PointOnObject(g18,g21)
    c: PointOnObject(g19,g21)
    c: PointOnObject(g20,g21)
    c: Coincident(g22,g23)
    c: Coincident(g23,g24)
    c: Coincident(g24,g25)
    c: Coincident(g25,g26)
    c: Coincident(g26,g27)
    c: Coincident(g27,g22)
    c: Equal(g22, g23-g27) x5
    c: PointOnObject(g22,g28)
    c: PointOnObject(g23,g28)
    c: PointOnObject(g24,g28)
    c: PointOnObject(g25,g28)
    c: PointOnObject(g26,g28)
    c: PointOnObject(g27,g28)
    c: DistanceX(g7,g14) = 71.5
    c: Symmetric(g7,g14,g-2)
    c: Symmetric(g7,g28,g-1)
    c: Symmetric(g28,g21,g-2)
    c: Horizontal(g6)
    c: Horizontal(g13)
    c: Horizontal(g27)
    c: Horizontal(g20)
    c: Equal(g6,g13)
    c: Equal(g13,g20)
    c: Equal(g20,g27)
    c: Distance(g5,g2) = 7.7
    c: DistanceY(g21,g14) = 71.5
FEATURE [Sketcher::SketchObject] Sketch086  label="sk_control_cutout"
  AttachmentOffset = pos=(0,-55,70.7107) rot=(0,0,1;0rad)
  FullyConstrained = true
  MapMode = 5
  Placement = pos=(70.7107,-2.79e-14,-55) rot=(0.57735,0.57735,0.57735;2.0944rad)
  Support = -> [YZ_Plane014]
  expr: .AttachmentOffset.Base.y = -<<Spreadsheet>>.fan_duct_depth + <<Spreadsheet>>.fan_mount_overhang - <<Spreadsheet>>.fan_mount_depth / 2
  expr: .AttachmentOffset.Base.z = <<Spreadsheet>>.fan_mount_outer_radius
  sketch-geometry (4):
    g0: LineSegment StartX=-25 StartY=12.98 StartZ=0 EndX=25 EndY=12.98 EndZ=0
    g1: LineSegment StartX=25 StartY=12.98 StartZ=0 EndX=25 EndY=-12.98 EndZ=0
    g2: LineSegment StartX=25 StartY=-12.98 StartZ=0 EndX=-25 EndY=-12.98 EndZ=0
    g3: LineSegment StartX=-25 StartY=-12.98 StartZ=0 EndX=-25 EndY=12.98 EndZ=0
  constraints (10):
    c: Coincident(g0,g1)
    c: Coincident(g1,g2)
    c: Coincident(g2,g3)
    c: Coincident(g3,g0)
    c: Horizontal(g0)
    c: Vertical(g3)
    c: Symmetric(g0,g1,g-1)
    c: Symmetric(g1,g2,g-2)
    c: DistanceY(g3,g3) = 25.96
    c: DistanceX(g0,g0) = 50
FEATURE [PartDesign::Pocket] Pocket003030  label="pocket_control_cutout"
  BaseFeature = -> Pocket003029
  Direction = (-1,2e-16,-3e-16)
  Length = 15
  Length2 = 5
  Profile = -> Sketch086
  ReferenceAxis = -> Sketch086 [N_Axis]
  Refine = true
  Type = 0
FEATURE [PartDesign::Pocket] Pocket003031  label="pocket_fan_mounting_nuts"
  BaseFeature = -> Pocket003030
  Direction = (0,0,-1)
  Length = 3.2
  Length2 = 5
  Profile = -> Sketch085
  ReferenceAxis = -> Sketch085 [N_Axis]
  Refine = true
  Reversed = true
  Type = 0
  expr: Length = <<Spreadsheet>>.m4_nut_depth
FEATURE [Sketcher::SketchObject] Sketch087  label="sk_fan_mount_hole_screw_inlay"
  AttachmentOffset = pos=(0,0,-20) rot=(0,0,1;0rad)
  FullyConstrained = true
  MapMode = 5
  Placement = pos=(0,0,-20) rot=(0,0,1;0rad)
  Support = -> [XY_Plane014]
  expr: .AttachmentOffset.Base.z = -<<Spreadsheet>>.fan_duct_depth + <<Spreadsheet>>.fan_mount_overhang + 10mm
  expr: .Constraints.mounting_hole_diameter = <<Spreadsheet>>.fan_mount_hole_screw_inlay
  expr: .Constraints.mounting_holes_distance = <<Spreadsheet>>.fan_mounting_hole_distance
  expr: Constraints[6] = .Constraints.mounting_holes_distance
  sketch-geometry (5):
    g0: GeomPoint X=0 Y=0 Z=0
    g1: Circle CenterX=-35.75 CenterY=35.75 CenterZ=0 NormalX=0 NormalY=0 NormalZ=1 AngleXU=0 Radius=4
    g2: Circle CenterX=35.75 CenterY=35.75 CenterZ=0 NormalX=0 NormalY=0 NormalZ=1 AngleXU=0 Radius=4
    g3: Circle CenterX=35.75 CenterY=-35.75 CenterZ=0 NormalX=0 NormalY=0 NormalZ=1 AngleXU=0 Radius=4
    g4: Circle CenterX=-35.75 CenterY=-35.75 CenterZ=0 NormalX=0 NormalY=0 NormalZ=1 AngleXU=0 Radius=4
  constraints (10):
    c: Coincident(g0,g-1)
    c: Equal(g4,g3)
    c: Equal(g3,g2)
    c: Equal(g2,g1)
    c: Symmetric(g3,g4,g-2)
    c: DistanceX(g1,g2) = 71.5  'mounting_holes_distance'
    c: DistanceY(g3,g2) = 71.5
    c: Diameter(g1) = 8  'mounting_hole_diameter'
    c: Symmetric(g4,g2,g0)
    c: Symmetric(g1,g3,g0)
FEATURE [PartDesign::Pocket] Pocket003032  label="pocket_fan_mount_hole_screw_inlay"
  BaseFeature = -> Pocket003031
  Direction = (0,0,-1)
  Length = 0
  Length2 = 5
  Profile = -> Sketch087
  ReferenceAxis = -> Sketch087 [N_Axis]
  Refine = true
  Reversed = true
  Type = 1
FEATURE [PartDesign::Body] Body014
  Group = -> [Sketch070,Sketch071,Pad027,Pocket003027,Sketch073,Sketch074,Sketch075,AdditiveLoft004,Sketch083,Pad028,Sketch084,Pocket003028,Pocket003029,Sketch085,Sketch086,Pocket003030,Pocket003031,Sketch087,Pocket003032]
  Origin = -> Origin014
  Placement = pos=(0,0,-111) rot=(0,0,1;0rad)
  Tip = -> Pocket003032
FEATURE [Sketcher::SketchObject] Sketch  label="sk_fanduct_base"
  FullyConstrained = true
  MapMode = 5
  Support = -> [XY_Plane]
  expr: Constraints[20] = .Constraints.mounting_holes_distance
  sketch-geometry (10):
    g0: LineSegment StartX=-41 StartY=-41 StartZ=0 EndX=-41 EndY=41 EndZ=0
    g1: LineSegment StartX=-41 StartY=41 StartZ=0 EndX=41 EndY=41 EndZ=0
    g2: LineSegment StartX=41 StartY=41 StartZ=0 EndX=41 EndY=-41 EndZ=0
    g3: LineSegment StartX=41 StartY=-41 StartZ=0 EndX=-41 EndY=-41 EndZ=0
    g4: GeomPoint X=0 Y=0 Z=0
    g5: Circle CenterX=0 CenterY=0 CenterZ=0 NormalX=0 NormalY=0 NormalZ=1 AngleXU=0 Radius=38.15
    g6: Circle CenterX=-35.75 CenterY=35.75 CenterZ=0 NormalX=0 NormalY=0 NormalZ=1 AngleXU=0 Radius=2.15
    g7: Circle CenterX=35.75 CenterY=35.75 CenterZ=0 NormalX=0 NormalY=0 NormalZ=1 AngleXU=0 Radius=2.15
    g8: Circle CenterX=35.75 CenterY=-35.75 CenterZ=0 NormalX=0 NormalY=0 NormalZ=1 AngleXU=0 Radius=2.15
    g9: Circle CenterX=-35.75 CenterY=-35.75 CenterZ=0 NormalX=0 NormalY=0 NormalZ=1 AngleXU=0 Radius=2.15
  constraints (23):
    c: Coincident(g0,g1)
    c: Coincident(g1,g2)
    c: Coincident(g2,g3)
    c: Coincident(g3,g0)
    c: Horizontal(g1)
    c: Horizontal(g3)
    c: Vertical(g0)
    c: Vertical(g2)
    c: Symmetric(g1,g0,g4)
    c: Coincident(g4,g-1)
    c: Equal(g1,g2)
    c: DistanceY(g2,g2) = 82  'fan_width'
    c: Coincident(g5,g4)
    c: Equal(g9,g8)
    c: Equal(g8,g7)
    c: Equal(g7,g6)
    c: Symmetric(g6,g8,g5)
    c: Symmetric(g7,g9,g5)
    c: Symmetric(g8,g9,g-2)
    c: DistanceX(g6,g7) = 71.5  'mounting_holes_distance'
    c: DistanceY(g8,g7) = 71.5
    c: Diameter(g6) = 4.3  'mounting_hole_diameter'
    c: Diameter(g5) = 76.3  'duct_hole_diameter'
FEATURE [PartDesign::Pad] Pad  label="pad_base"
  Direction = (0,0,1)
  Length = 10
  Length2 = 10
  Midplane = true
  Profile = -> Sketch
  Type = 0
FEATURE [Sketcher::SketchObject] Sketch001  label="sk_fanduct_to_pipe_1"
  AttachmentOffset = pos=(0,0,5) rot=(0,0,1;0rad)
  FullyConstrained = true
  MapMode = 5
  Placement = pos=(0,0,5) rot=(0,0,1;0rad)
  Support = -> [XY_Plane]
  expr: .AttachmentOffset.Base.z = <<pad_base>>.Length / 2
  expr: Constraints[12] = <<sk_fanduct_base>>.Constraints.fan_width
  expr: Constraints[1] = <<sk_fanduct_base>>.Constraints.duct_hole_diameter
  sketch-geometry (6):
    g0: Circle CenterX=0 CenterY=0 CenterZ=0 NormalX=0 NormalY=0 NormalZ=1 AngleXU=0 Radius=38.15
    g1: LineSegment StartX=-41 StartY=41 StartZ=0 EndX=-41 EndY=-41 EndZ=0
    g2: LineSegment StartX=-41 StartY=-41 StartZ=0 EndX=41 EndY=-41 EndZ=0
    g3: LineSegment StartX=41 StartY=-41 StartZ=0 EndX=41 EndY=41 EndZ=0
    g4: LineSegment StartX=41 StartY=41 StartZ=0 EndX=-41 EndY=41 EndZ=0
    g5: GeomPoint X=0 Y=0 Z=0
  constraints (14):
    c: Coincident(g0,g-1)
    c: Diameter(g0) = 76.3
    c: Coincident(g1,g2)
    c: Coincident(g2,g3)
    c: Coincident(g3,g4)
    c: Coincident(g4,g1)
    c: Horizontal(g2)
    c: Horizontal(g4)
    c: Vertical(g1)
    c: Vertical(g3)
    c: Symmetric(g2,g1,g5)
    c: Coincident(g5,g0)
    c: DistanceY(g3,g3) = 82
    c: Equal(g3,g2)
FEATURE [Sketcher::SketchObject] Sketch003  label="sk_pipe"
  AttachmentOffset = pos=(0,0,20) rot=(0,0,1;0rad)
  FullyConstrained = true
  MapMode = 5
  Placement = pos=(0,0,20) rot=(0,0,1;0rad)
  Support = -> [XY_Plane]
  expr: .AttachmentOffset.Base.z = <<sk_fanduct_to_pipe_2>>.Placement.Base.z
  expr: .Constraints.pipe_outer_diameter = <<sk_fanduct_base>>.Constraints.duct_hole_diameter + 4mm
  expr: Constraints[1] = <<sk_fanduct_base>>.Constraints.duct_hole_diameter
  sketch-geometry (2):
    g0: Circle CenterX=0 CenterY=0 CenterZ=0 NormalX=0 NormalY=0 NormalZ=1 AngleXU=0 Radius=38.15
    g1: Circle CenterX=0 CenterY=0 CenterZ=0 NormalX=0 NormalY=0 NormalZ=1 AngleXU=0 Radius=40.15
  constraints (4):
    c: Coincident(g0,g-1)
    c: Diameter(g0) = 76.3
    c: Coincident(g1,g0)
    c: Diameter(g1) = 80.3  'pipe_outer_diameter'
FEATURE [Sketcher::SketchObject] Sketch002  label="sk_fanduct_to_pipe_2"
  AttachmentOffset = pos=(0,0,20) rot=(0,0,1;0rad)
  FullyConstrained = true
  MapMode = 5
  Placement = pos=(0,0,20) rot=(0,0,1;0rad)
  Support = -> [XY_Plane]
  expr: .Constraints.pipe_outer_diameter = <<sk_fanduct_base>>.Constraints.duct_hole_diameter + 4mm
  expr: Constraints[1] = <<sk_fanduct_base>>.Constraints.duct_hole_diameter
  sketch-geometry (2):
    g0: Circle CenterX=0 CenterY=0 CenterZ=0 NormalX=0 NormalY=0 NormalZ=1 AngleXU=0 Radius=38.15
    g1: Circle CenterX=0 CenterY=0 CenterZ=0 NormalX=0 NormalY=0 NormalZ=1 AngleXU=0 Radius=40.15
  constraints (4):
    c: Coincident(g0,g-1)
    c: Diameter(g0) = 76.3
    c: Coincident(g1,g0)
    c: Diameter(g1) = 80.3  'pipe_outer_diameter'
FEATURE [PartDesign::AdditiveLoft] AdditiveLoft
  BaseFeature = -> Pad
  Closed = true
  Profile = -> Sketch001
  Refine = true
  Ruled = true
  Sections = -> [Sketch002]
  UpToFace = -> Sketch002
FEATURE [PartDesign::Pad] Pad013
  BaseFeature = -> AdditiveLoft
  Direction = (0,0,1)
  Length = 40
  Length2 = 10
  Profile = -> Sketch003
  Refine = true
  Type = 0
FEATURE [PartDesign::Body] Body  label="FanAdapter"
  Group = -> [Sketch,Pad,Sketch001,Sketch003,Sketch002,AdditiveLoft,Pad013]
  Origin = -> Origin
  Placement = pos=(0,0,-131) rot=(0,0,1;0rad)
  Tip = -> Pad013
